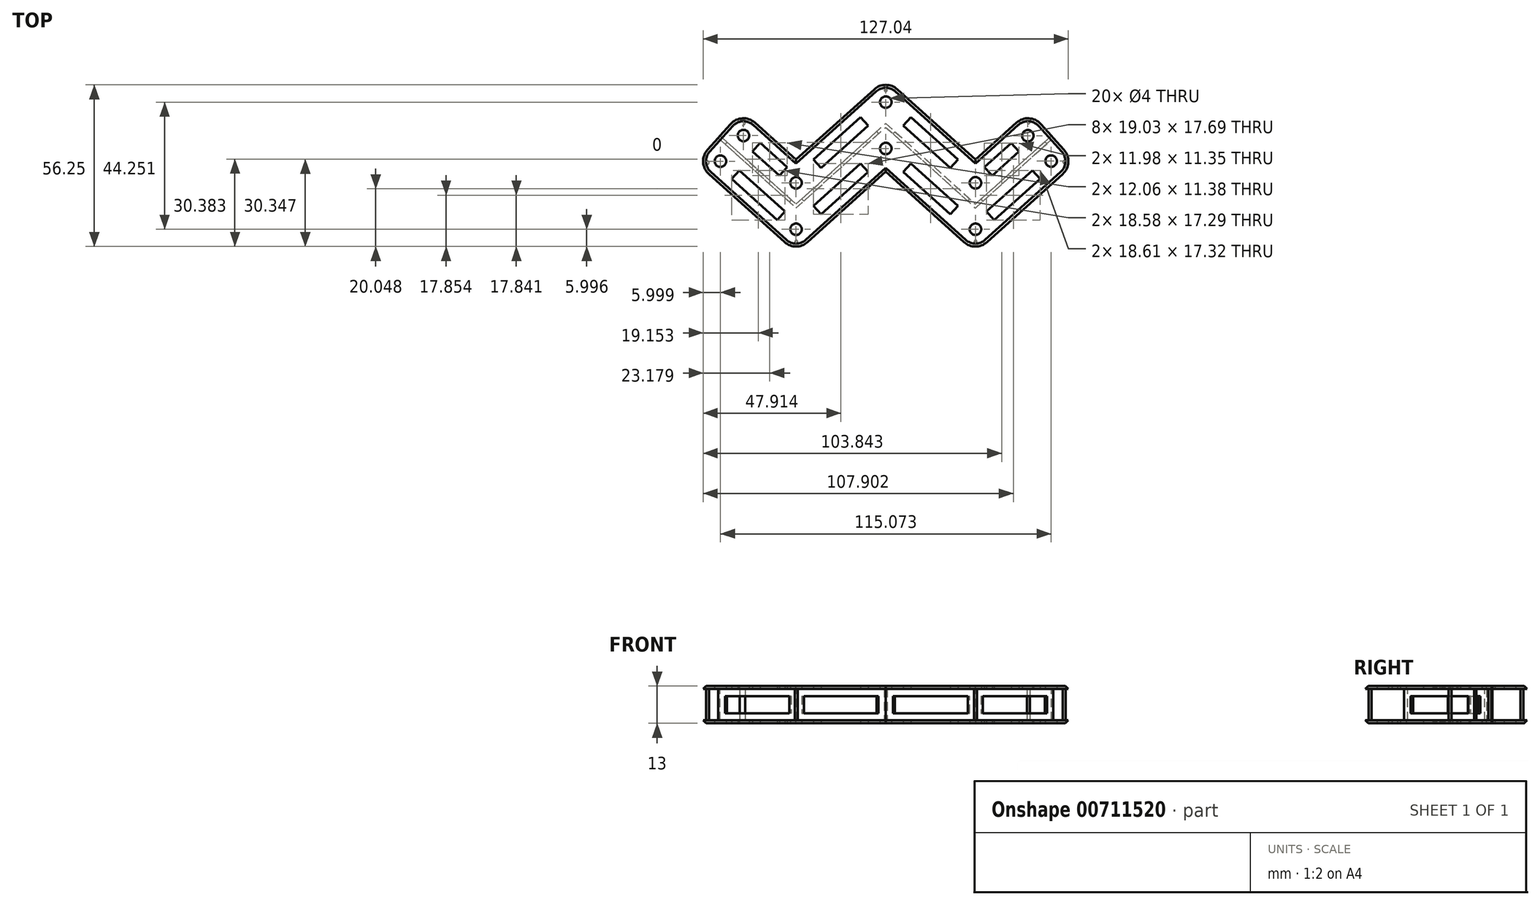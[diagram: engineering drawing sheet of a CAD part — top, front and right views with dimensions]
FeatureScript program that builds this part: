
annotation { "Feature Type Name" : "Feature", "Feature Type Description" : "" }
export const myFeature = defineFeature(function(context is Context, id is Id, definition is map)
    precondition{}
    {
        {
            var Q0;
            Q0=qCreatedBy(makeId("Top.planeOp"),FACE);
            var sketch = newSketch(context, id + "F0", { "sketchPlane" : qUnion([Q0]), "disableImprinting" : false});
            skLineSegment(sketch, "E0", {"start": v(-57.97, 24.09) * mm, "end": v(-31.21, 0) * mm});
            skLineSegment(sketch, "E1", {"start": v(-31.21, 0) * mm, "end": v(0, 28.1) * mm});
            skLineSegment(sketch, "E2", {"start": v(0, 28.1) * mm, "end": v(31.21, 0) * mm});
            skLineSegment(sketch, "E3", {"start": v(31.21, 0) * mm, "end": v(57.97, 24.09) * mm});
            skLineSegment(sketch, "E4.0", {"start": v(31.21, -0.67) * mm, "end": v(58.3, 23.72) * mm});
            skLineSegment(sketch, "E4.1", {"start": v(0, 27.43) * mm, "end": v(31.21, -0.67) * mm});
            skLineSegment(sketch, "E4.2", {"start": v(-31.21, -0.67) * mm, "end": v(0, 27.43) * mm});
            skLineSegment(sketch, "E4.3", {"start": v(-58.3, 23.72) * mm, "end": v(-31.21, -0.67) * mm});
            skLineSegment(sketch, "E5.0", {"start": v(31.21, 0.67) * mm, "end": v(57.63, 24.46) * mm});
            skLineSegment(sketch, "E5.1", {"start": v(0, 28.78) * mm, "end": v(31.21, 0.67) * mm});
            skLineSegment(sketch, "E5.2", {"start": v(-31.21, 0.67) * mm, "end": v(0, 28.78) * mm});
            skLineSegment(sketch, "E5.3", {"start": v(-57.63, 24.46) * mm, "end": v(-31.21, 0.67) * mm});
            skLineSegment(sketch, "E6", {"start": v(-58.3, 23.72) * mm, "end": v(-57.97, 24.09) * mm});
            skLineSegment(sketch, "E7", {"start": v(-57.97, 24.09) * mm, "end": v(-57.63, 24.46) * mm});
            skLineSegment(sketch, "E8", {"start": v(57.63, 24.46) * mm, "end": v(57.97, 24.09) * mm});
            skLineSegment(sketch, "E9", {"start": v(58.3, 23.72) * mm, "end": v(57.97, 24.09) * mm});
            skLineSegment(sketch, "E10.0", {"start": v(31.21, -16.15) * mm, "end": v(66, 15.17) * mm});
            skLineSegment(sketch, "E10.1", {"start": v(0, 11.96) * mm, "end": v(31.21, -16.15) * mm});
            skLineSegment(sketch, "E10.2", {"start": v(-31.21, -16.15) * mm, "end": v(0, 11.96) * mm});
            skLineSegment(sketch, "E10.3", {"start": v(-66, 15.17) * mm, "end": v(-31.21, -16.15) * mm});
            skLineSegment(sketch, "E11.0", {"start": v(31.21, 16.15) * mm, "end": v(49.94, 33) * mm});
            skLineSegment(sketch, "E11.1", {"start": v(0, 44.25) * mm, "end": v(31.21, 16.15) * mm});
            skLineSegment(sketch, "E11.2", {"start": v(-31.21, 16.15) * mm, "end": v(0, 44.25) * mm});
            skLineSegment(sketch, "E11.3", {"start": v(-49.94, 33) * mm, "end": v(-31.21, 16.15) * mm});
            skLineSegment(sketch, "E12", {"start": v(-66, 15.17) * mm, "end": v(-58.3, 23.72) * mm});
            skLineSegment(sketch, "E13", {"start": v(-49.94, 33) * mm, "end": v(-57.63, 24.46) * mm});
            skLineSegment(sketch, "E14", {"start": v(66, 15.17) * mm, "end": v(58.3, 23.72) * mm});
            skLineSegment(sketch, "E15", {"start": v(49.94, 33) * mm, "end": v(57.63, 24.46) * mm});
            skLineSegment(sketch, "E16.0", {"start": v(31.21, -8.07) * mm, "end": v(62.01, 19.66) * mm, "construction": true});
            skLineSegment(sketch, "E16.1", {"start": v(0, 20.03) * mm, "end": v(31.21, -8.07) * mm, "construction": true});
            skLineSegment(sketch, "E16.2", {"start": v(-31.21, -8.07) * mm, "end": v(0, 20.03) * mm, "construction": true});
            skLineSegment(sketch, "E16.3", {"start": v(-61.98, 19.63) * mm, "end": v(-31.21, -8.07) * mm, "construction": true});
            skLineSegment(sketch, "E17.0", {"start": v(31.21, 8.07) * mm, "end": v(53.9, 28.5) * mm, "construction": true});
            skLineSegment(sketch, "E17.1", {"start": v(0, 36.18) * mm, "end": v(31.21, 8.07) * mm, "construction": true});
            skLineSegment(sketch, "E17.2", {"start": v(-31.21, 8.07) * mm, "end": v(0, 36.18) * mm, "construction": true});
            skLineSegment(sketch, "E17.3", {"start": v(-53.95, 28.55) * mm, "end": v(-31.21, 8.07) * mm, "construction": true});
            skCircle(sketch, "E18", {"center": v(-31.21, 8.07) * mm, "radius": 2 * mm});
            skCircle(sketch, "E19", {"center": v(-31.21, -8.07) * mm, "radius": 2 * mm});
            skCircle(sketch, "E20", {"center": v(0, 20.03) * mm, "radius": 2 * mm});
            skCircle(sketch, "E21", {"center": v(0, 36.18) * mm, "radius": 2 * mm});
            skCircle(sketch, "E22", {"center": v(31.21, 8.07) * mm, "radius": 2 * mm});
            skCircle(sketch, "E23", {"center": v(31.21, -8.07) * mm, "radius": 2 * mm});
            skCircle(sketch, "E24", {"center": v(49.43, 24.48) * mm, "radius": 2 * mm});
            skCircle(sketch, "E25", {"center": v(57.55, 15.64) * mm, "radius": 2 * mm});
            skCircle(sketch, "E26", {"center": v(-57.52, 15.62) * mm, "radius": 2 * mm});
            skCircle(sketch, "E27", {"center": v(-49.5, 24.53) * mm, "radius": 2 * mm});
            skLineSegment(sketch, "E28.0", {"start": v(31.21, -10.77) * mm, "end": v(63.32, 18.14) * mm, "construction": true});
            skLineSegment(sketch, "E28.1", {"start": v(0, 17.34) * mm, "end": v(31.21, -10.77) * mm, "construction": true});
            skLineSegment(sketch, "E28.2", {"start": v(-31.21, -10.77) * mm, "end": v(0, 17.34) * mm, "construction": true});
            skLineSegment(sketch, "E28.3", {"start": v(-63.32, 18.14) * mm, "end": v(-31.21, -10.77) * mm, "construction": true});
            skLineSegment(sketch, "E29.0", {"start": v(31.21, -5.38) * mm, "end": v(60.64, 21.12) * mm, "construction": true});
            skLineSegment(sketch, "E29.1", {"start": v(0, 22.72) * mm, "end": v(31.21, -5.38) * mm, "construction": true});
            skLineSegment(sketch, "E29.2", {"start": v(-31.21, -5.38) * mm, "end": v(0, 22.72) * mm, "construction": true});
            skLineSegment(sketch, "E29.3", {"start": v(-60.64, 21.12) * mm, "end": v(-31.21, -5.38) * mm, "construction": true});
            skLineSegment(sketch, "E30.0", {"start": v(31.21, 10.77) * mm, "end": v(52.61, 30.03) * mm, "construction": true});
            skLineSegment(sketch, "E30.1", {"start": v(0, 38.87) * mm, "end": v(31.21, 10.77) * mm, "construction": true});
            skLineSegment(sketch, "E30.2", {"start": v(-31.21, 10.77) * mm, "end": v(0, 38.87) * mm, "construction": true});
            skLineSegment(sketch, "E30.3", {"start": v(-52.61, 30.03) * mm, "end": v(-31.21, 10.77) * mm, "construction": true});
            skLineSegment(sketch, "E31.0", {"start": v(31.21, 5.38) * mm, "end": v(55.29, 27.06) * mm, "construction": true});
            skLineSegment(sketch, "E31.1", {"start": v(0, 33.49) * mm, "end": v(31.21, 5.38) * mm, "construction": true});
            skLineSegment(sketch, "E31.2", {"start": v(-31.21, 5.38) * mm, "end": v(0, 33.49) * mm, "construction": true});
            skLineSegment(sketch, "E31.3", {"start": v(-55.29, 27.06) * mm, "end": v(-31.21, 5.38) * mm, "construction": true});
            skLineSegment(sketch, "E32", {"start": v(-25.12, 16.25) * mm, "end": v(-8.77, 30.97) * mm});
            skLineSegment(sketch, "E33", {"start": v(-8.77, 30.97) * mm, "end": v(-6.1, 28) * mm});
            skLineSegment(sketch, "E34", {"start": v(-25.12, 16.25) * mm, "end": v(-22.44, 13.28) * mm});
            skLineSegment(sketch, "E35", {"start": v(-22.44, 13.28) * mm, "end": v(-6.1, 28) * mm});
            skLineSegment(sketch, "E36", {"start": v(-43.7, 22) * mm, "end": v(-46.37, 19.03) * mm});
            skLineSegment(sketch, "E37", {"start": v(-46.37, 19.03) * mm, "end": v(-37.03, 10.62) * mm});
            skLineSegment(sketch, "E38", {"start": v(-37.03, 10.62) * mm, "end": v(-34.31, 13.56) * mm});
            skLineSegment(sketch, "E39", {"start": v(-34.31, 13.56) * mm, "end": v(-43.7, 22) * mm});
            skLineSegment(sketch, "E40", {"start": v(-50.98, 12.42) * mm, "end": v(-53.66, 9.44) * mm});
            skLineSegment(sketch, "E41", {"start": v(-53.66, 9.44) * mm, "end": v(-37.75, -4.88) * mm});
            skLineSegment(sketch, "E42", {"start": v(-37.75, -4.88) * mm, "end": v(-35.08, -1.9) * mm});
            skLineSegment(sketch, "E43", {"start": v(-35.08, -1.9) * mm, "end": v(-50.98, 12.42) * mm});
            skLineSegment(sketch, "E44", {"start": v(-22.44, -2.87) * mm, "end": v(-25.12, 0.1) * mm});
            skLineSegment(sketch, "E45", {"start": v(-25.12, 0.1) * mm, "end": v(-8.77, 14.82) * mm});
            skLineSegment(sketch, "E46", {"start": v(-8.77, 14.82) * mm, "end": v(-6.1, 11.85) * mm});
            skLineSegment(sketch, "E47", {"start": v(-6.1, 11.85) * mm, "end": v(-22.44, -2.87) * mm});
            skLineSegment(sketch, "E48", {"start": v(8.77, 30.97) * mm, "end": v(6.1, 28) * mm});
            skLineSegment(sketch, "E49", {"start": v(6.1, 28) * mm, "end": v(22.44, 13.28) * mm});
            skLineSegment(sketch, "E50", {"start": v(22.44, 13.28) * mm, "end": v(25.12, 16.25) * mm});
            skLineSegment(sketch, "E51", {"start": v(25.12, 16.25) * mm, "end": v(8.77, 30.97) * mm});
            skLineSegment(sketch, "E52", {"start": v(6.1, 11.85) * mm, "end": v(8.77, 14.82) * mm});
            skLineSegment(sketch, "E53", {"start": v(8.77, 14.82) * mm, "end": v(25.12, 0.1) * mm});
            skLineSegment(sketch, "E54", {"start": v(25.12, 0.1) * mm, "end": v(22.44, -2.87) * mm});
            skLineSegment(sketch, "E55", {"start": v(22.44, -2.87) * mm, "end": v(6.1, 11.85) * mm});
            skLineSegment(sketch, "E56", {"start": v(34.33, 13.57) * mm, "end": v(37, 10.6) * mm});
            skLineSegment(sketch, "E57", {"start": v(37, 10.6) * mm, "end": v(46.31, 18.98) * mm});
            skLineSegment(sketch, "E58", {"start": v(46.31, 18.98) * mm, "end": v(43.64, 21.95) * mm});
            skLineSegment(sketch, "E59", {"start": v(43.64, 21.95) * mm, "end": v(34.33, 13.57) * mm});
            skLineSegment(sketch, "E60", {"start": v(35.08, -1.9) * mm, "end": v(37.75, -4.88) * mm});
            skLineSegment(sketch, "E61", {"start": v(37.75, -4.88) * mm, "end": v(53.69, 9.47) * mm});
            skLineSegment(sketch, "E62", {"start": v(53.69, 9.47) * mm, "end": v(51.01, 12.44) * mm});
            skLineSegment(sketch, "E63", {"start": v(51.01, 12.44) * mm, "end": v(35.08, -1.9) * mm});
            skCircle(sketch, "E64", {"center": v(-61.95, 15.13) * mm, "radius": 0.5 * mm});
            skCircle(sketch, "E65", {"center": v(-49.87, 29.1) * mm, "radius": 1 * mm});
            skCircle(sketch, "E66", {"center": v(-31.12, -12.42) * mm, "radius": 0.5 * mm});
            skCircle(sketch, "E67", {"center": v(0, 40.35) * mm, "radius": 0.5 * mm});
            skCircle(sketch, "E68", {"center": v(31.26, -12.4) * mm, "radius": 0.5 * mm});
            skCircle(sketch, "E69", {"center": v(62.1, 15.36) * mm, "radius": 0.5 * mm});
            skCircle(sketch, "E70", {"center": v(49.66, 29.19) * mm, "radius": 0.5 * mm});
            skSolve(sketch);
        }
        {
            var Q0;
            Q0=makeQuery(id+"F0.imprint","IMPRINT",FACE,{"disambiguationData":[TD([[makeQuery(id+"F0.imprint","IMPRINT",EDGE,{"derivedFrom":sQuery(id+"F0.wireOp",EDGE,"E5.0")}),1.0]])]});
            var Q1;
            Q1=makeQuery(id+"F0.imprint","IMPRINT",FACE,{"disambiguationData":[TD([[makeQuery(id+"F0.imprint","IMPRINT",EDGE,{"derivedFrom":sQuery(id+"F0.wireOp",EDGE,"E4.0")}),-1.0]])]});
            var Q2;
            Q2=makeQuery(id+"F0.imprint","IMPRINT",FACE,{"disambiguationData":[TD([[makeQuery(id+"F0.imprint","IMPRINT",EDGE,{"derivedFrom":sQuery(id+"F0.wireOp",EDGE,"E0")}),1.0]])]});
            var Q3;
            Q3=makeQuery(id+"F0.imprint","IMPRINT",FACE,{"disambiguationData":[TD([[makeQuery(id+"F0.imprint","IMPRINT",EDGE,{"derivedFrom":sQuery(id+"F0.wireOp",EDGE,"E0")}),-1.0]])]});
            extrude(context, id + "F1", {"entities" : qUnion([Q0, Q1, Q2, Q3]), "depth" : 13 * mm, "offsetDistance" : 25 * mm, "symmetric" : true});
        }
        {
            var Q0;
            Q0=makeQuery(id+"F0.imprint","IMPRINT",FACE,{"disambiguationData":[TD([[makeQuery(id+"F0.imprint","IMPRINT",EDGE,{"derivedFrom":sQuery(id+"F0.wireOp",EDGE,"E5.0")}),1.0]])]});
            var Q1;
            Q1=makeQuery(id+"F0.imprint","IMPRINT",FACE,{"disambiguationData":[TD([[makeQuery(id+"F0.imprint","IMPRINT",EDGE,{"derivedFrom":sQuery(id+"F0.wireOp",EDGE,"E4.0")}),-1.0]])]});
            extrude(context, id + "F2", {"entities" : qUnion([Q0, Q1]), "operationType" : NewBodyOperationType.REMOVE, "oppositeDirection" : true, "depth" : 11 * mm, "offsetDistance" : 25 * mm, "symmetric" : true});
        }
        {
            var Q0;
            Q0=makeQuery(id+"F2.boolean.opBoolean","COPY",FACE,{"derivedFrom":makeQuery(id+"F2.opExtrude","SWEPT_FACE",FACE,{"disambiguationData":[OSD([sQuery(id+"F0.wireOp",EDGE,"E4.0")])]})});
            var sketch = newSketch(context, id + "F3", { "sketchPlane" : qUnion([Q0])});
            skLineSegment(sketch, "E71.bottom", {"start": v(26.18, 3) * mm, "end": v(56.18, 3) * mm});
            skLineSegment(sketch, "E71.top", {"start": v(26.18, -3) * mm, "end": v(56.18, -3) * mm});
            skLineSegment(sketch, "E71.left", {"start": v(26.18, 3) * mm, "end": v(26.18, -3) * mm});
            skLineSegment(sketch, "E71.right", {"start": v(56.18, 3) * mm, "end": v(56.18, -3) * mm});
            skPoint(sketch, "E71.middle", {"position": v(41.18, 0) * mm});
            skSolve(sketch);
        }
        {
            var Q0;
            Q0=makeQuery(id+"F3.imprint","IMPRINT",FACE,{"disambiguationData":[TD([[makeQuery(id+"F3.imprint","IMPRINT",EDGE,{"derivedFrom":sQuery(id+"F3.wireOp",EDGE,"E71.bottom")}),-1.0]])]});
            extrude(context, id + "F4", {"entities" : qUnion([Q0]), "operationType" : NewBodyOperationType.REMOVE, "oppositeDirection" : true, "depth" : 2 * mm, "offsetDistance" : 25 * mm, "symmetric" : true});
        }
        {
            var Q0;
            Q0=makeQuery(id+"F2.boolean.opBoolean","COPY",FACE,{"derivedFrom":makeQuery(id+"F2.opExtrude","SWEPT_FACE",FACE,{"disambiguationData":[OSD([sQuery(id+"F0.wireOp",EDGE,"E5.1")])]})});
            var sketch = newSketch(context, id + "F5", { "sketchPlane" : qUnion([Q0])});
            skLineSegment(sketch, "E72.bottom", {"start": v(-20.04, 3) * mm, "end": v(14.96, 3) * mm});
            skLineSegment(sketch, "E72.top", {"start": v(-20.04, -3) * mm, "end": v(14.96, -3) * mm});
            skLineSegment(sketch, "E72.left", {"start": v(-20.04, 3) * mm, "end": v(-20.04, -3) * mm});
            skLineSegment(sketch, "E72.right", {"start": v(14.96, 3) * mm, "end": v(14.96, -3) * mm});
            skPoint(sketch, "E72.middle", {"position": v(-2.54, 0) * mm});
            skSolve(sketch);
        }
        {
            var Q0;
            Q0=makeQuery(id+"F5.imprint","IMPRINT",FACE,{"disambiguationData":[TD([[makeQuery(id+"F5.imprint","IMPRINT",EDGE,{"derivedFrom":sQuery(id+"F5.wireOp",EDGE,"E72.bottom")}),-1.0]])]});
            extrude(context, id + "F6", {"entities" : qUnion([Q0]), "operationType" : NewBodyOperationType.REMOVE, "oppositeDirection" : true, "depth" : 3 * mm, "offsetDistance" : 25 * mm, "symmetric" : true});
        }
        {
            var Q0;
            Q0=makeQuery(id+"F2.boolean.opBoolean","COPY",FACE,{"derivedFrom":makeQuery(id+"F2.opExtrude","SWEPT_FACE",FACE,{"disambiguationData":[OSD([sQuery(id+"F0.wireOp",EDGE,"E4.2")])]})});
            var sketch = newSketch(context, id + "F7", { "sketchPlane" : qUnion([Q0])});
            skLineSegment(sketch, "E73.bottom", {"start": v(-20, 3) * mm, "end": v(15, 3) * mm});
            skLineSegment(sketch, "E73.top", {"start": v(-20, -3) * mm, "end": v(15, -3) * mm});
            skLineSegment(sketch, "E73.left", {"start": v(-20, 3) * mm, "end": v(-20, -3) * mm});
            skLineSegment(sketch, "E73.right", {"start": v(15, 3) * mm, "end": v(15, -3) * mm});
            skPoint(sketch, "E73.middle", {"position": v(-2.5, 0) * mm});
            skSolve(sketch);
        }
        {
            var Q0;
            Q0=makeQuery(id+"F7.imprint","IMPRINT",FACE,{"disambiguationData":[TD([[makeQuery(id+"F7.imprint","IMPRINT",EDGE,{"derivedFrom":sQuery(id+"F7.wireOp",EDGE,"E73.bottom")}),-1.0]])]});
            extrude(context, id + "F8", {"entities" : qUnion([Q0]), "operationType" : NewBodyOperationType.REMOVE, "oppositeDirection" : true, "depth" : 3 * mm, "offsetDistance" : 25 * mm, "symmetric" : true});
        }
        {
            var Q0;
            Q0=makeQuery(id+"F2.boolean.opBoolean","COPY",FACE,{"derivedFrom":makeQuery(id+"F2.opExtrude","SWEPT_FACE",FACE,{"disambiguationData":[OSD([sQuery(id+"F0.wireOp",EDGE,"E4.3")])]})});
            var sketch = newSketch(context, id + "F9", { "sketchPlane" : qUnion([Q0])});
            skLineSegment(sketch, "E74.bottom", {"start": v(-55.95, 3) * mm, "end": v(-25.95, 3) * mm});
            skLineSegment(sketch, "E74.top", {"start": v(-55.95, -3) * mm, "end": v(-25.95, -3) * mm});
            skLineSegment(sketch, "E74.left", {"start": v(-55.95, 3) * mm, "end": v(-55.95, -3) * mm});
            skLineSegment(sketch, "E74.right", {"start": v(-25.95, 3) * mm, "end": v(-25.95, -3) * mm});
            skPoint(sketch, "E74.middle", {"position": v(-40.95, 0) * mm});
            skSolve(sketch);
        }
        {
            var Q0;
            Q0=makeQuery(id+"F9.imprint","IMPRINT",FACE,{"disambiguationData":[TD([[makeQuery(id+"F9.imprint","IMPRINT",EDGE,{"derivedFrom":sQuery(id+"F9.wireOp",EDGE,"E74.bottom")}),-1.0]])]});
            extrude(context, id + "F10", {"entities" : qUnion([Q0]), "operationType" : NewBodyOperationType.REMOVE, "oppositeDirection" : true, "depth" : 3 * mm, "offsetDistance" : 25 * mm, "symmetric" : true});
        }
        {
            var Q0;
            {var subQ0=sQuery(id+"F0.wireOp",EDGE,"E27");var subQ1=sQuery(id+"F0.wireOp",EDGE,"E24");var subQ2=sQuery(id+"F0.wireOp",EDGE,"E22");var subQ3=sQuery(id+"F0.wireOp",EDGE,"E21");var subQ4=sQuery(id+"F0.wireOp",EDGE,"E18");var subQ5=sQuery(id+"F0.wireOp",EDGE,"E15");var subQ7=sQuery(id+"F0.wireOp",EDGE,"E13");var subQ8=sQuery(id+"F0.wireOp",EDGE,"E11.3");var subQ9=sQuery(id+"F0.wireOp",EDGE,"E11.2");var subQ10=sQuery(id+"F0.wireOp",EDGE,"E11.1");var subQ11=sQuery(id+"F0.wireOp",EDGE,"E11.0");Q0=makeQuery(id+"F2.boolean.opBoolean","SPLIT",EDGE,{"disambiguationData":[TD([makeQuery(id+"F2.opExtrude","CAP_FACE",FACE,{"disambiguationData":[OSD([sQuery(id+"F0.wireOp",EDGE,"E5.0"),sQuery(id+"F0.wireOp",EDGE,"E5.1"),sQuery(id+"F0.wireOp",EDGE,"E5.2"),sQuery(id+"F0.wireOp",EDGE,"E5.3"),subQ11,subQ10,subQ9,subQ8,subQ7,subQ5,subQ4,subQ3,subQ2,subQ1,subQ0])],"isStart":true})])],"derivedFrom":makeQuery(id+"F1.opExtrude","SWEPT_EDGE",EDGE,{"disambiguationData":[OSD([subQ11,subQ5])]})});}
            var Q1;
            {var subQ0=sQuery(id+"F0.wireOp",EDGE,"E27");var subQ1=sQuery(id+"F0.wireOp",EDGE,"E24");var subQ2=sQuery(id+"F0.wireOp",EDGE,"E22");var subQ3=sQuery(id+"F0.wireOp",EDGE,"E21");var subQ4=sQuery(id+"F0.wireOp",EDGE,"E18");var subQ5=sQuery(id+"F0.wireOp",EDGE,"E15");var subQ7=sQuery(id+"F0.wireOp",EDGE,"E13");var subQ8=sQuery(id+"F0.wireOp",EDGE,"E11.3");var subQ9=sQuery(id+"F0.wireOp",EDGE,"E11.2");var subQ10=sQuery(id+"F0.wireOp",EDGE,"E11.1");var subQ11=sQuery(id+"F0.wireOp",EDGE,"E11.0");Q1=makeQuery(id+"F2.boolean.opBoolean","SPLIT",EDGE,{"disambiguationData":[TD([makeQuery(id+"F2.opExtrude","CAP_FACE",FACE,{"disambiguationData":[OSD([sQuery(id+"F0.wireOp",EDGE,"E5.0"),sQuery(id+"F0.wireOp",EDGE,"E5.1"),sQuery(id+"F0.wireOp",EDGE,"E5.2"),sQuery(id+"F0.wireOp",EDGE,"E5.3"),subQ11,subQ10,subQ9,subQ8,subQ7,subQ5,subQ4,subQ3,subQ2,subQ1,subQ0])],"isStart":false})])],"derivedFrom":makeQuery(id+"F1.opExtrude","SWEPT_EDGE",EDGE,{"disambiguationData":[OSD([subQ11,subQ5])]})});}
            var Q2;
            {var subQ0=sQuery(id+"F0.wireOp",EDGE,"E27");var subQ1=sQuery(id+"F0.wireOp",EDGE,"E24");var subQ2=sQuery(id+"F0.wireOp",EDGE,"E22");var subQ3=sQuery(id+"F0.wireOp",EDGE,"E21");var subQ4=sQuery(id+"F0.wireOp",EDGE,"E18");var subQ5=sQuery(id+"F0.wireOp",EDGE,"E15");var subQ6=sQuery(id+"F0.wireOp",EDGE,"E13");var subQ7=sQuery(id+"F0.wireOp",EDGE,"E11.3");var subQ8=sQuery(id+"F0.wireOp",EDGE,"E11.2");var subQ9=sQuery(id+"F0.wireOp",EDGE,"E11.1");var subQ10=sQuery(id+"F0.wireOp",EDGE,"E11.0");Q2=makeQuery(id+"F2.boolean.opBoolean","SPLIT",EDGE,{"disambiguationData":[TD([makeQuery(id+"F2.opExtrude","CAP_FACE",FACE,{"disambiguationData":[OSD([sQuery(id+"F0.wireOp",EDGE,"E5.0"),sQuery(id+"F0.wireOp",EDGE,"E5.1"),sQuery(id+"F0.wireOp",EDGE,"E5.2"),sQuery(id+"F0.wireOp",EDGE,"E5.3"),subQ10,subQ9,subQ8,subQ7,subQ6,subQ5,subQ4,subQ3,subQ2,subQ1,subQ0])],"isStart":false})])],"derivedFrom":makeQuery(id+"F1.opExtrude","SWEPT_EDGE",EDGE,{"disambiguationData":[OSD([subQ9,subQ8])]})});}
            var Q3;
            {var subQ0=sQuery(id+"F0.wireOp",EDGE,"E27");var subQ1=sQuery(id+"F0.wireOp",EDGE,"E24");var subQ2=sQuery(id+"F0.wireOp",EDGE,"E22");var subQ3=sQuery(id+"F0.wireOp",EDGE,"E21");var subQ4=sQuery(id+"F0.wireOp",EDGE,"E18");var subQ5=sQuery(id+"F0.wireOp",EDGE,"E15");var subQ6=sQuery(id+"F0.wireOp",EDGE,"E13");var subQ7=sQuery(id+"F0.wireOp",EDGE,"E11.3");var subQ8=sQuery(id+"F0.wireOp",EDGE,"E11.2");var subQ9=sQuery(id+"F0.wireOp",EDGE,"E11.1");var subQ10=sQuery(id+"F0.wireOp",EDGE,"E11.0");Q3=makeQuery(id+"F2.boolean.opBoolean","SPLIT",EDGE,{"disambiguationData":[TD([makeQuery(id+"F2.opExtrude","CAP_FACE",FACE,{"disambiguationData":[OSD([sQuery(id+"F0.wireOp",EDGE,"E5.0"),sQuery(id+"F0.wireOp",EDGE,"E5.1"),sQuery(id+"F0.wireOp",EDGE,"E5.2"),sQuery(id+"F0.wireOp",EDGE,"E5.3"),subQ10,subQ9,subQ8,subQ7,subQ6,subQ5,subQ4,subQ3,subQ2,subQ1,subQ0])],"isStart":true})])],"derivedFrom":makeQuery(id+"F1.opExtrude","SWEPT_EDGE",EDGE,{"disambiguationData":[OSD([subQ9,subQ8])]})});}
            var Q4;
            {var subQ0=sQuery(id+"F0.wireOp",EDGE,"E27");var subQ1=sQuery(id+"F0.wireOp",EDGE,"E24");var subQ2=sQuery(id+"F0.wireOp",EDGE,"E22");var subQ3=sQuery(id+"F0.wireOp",EDGE,"E21");var subQ4=sQuery(id+"F0.wireOp",EDGE,"E18");var subQ5=sQuery(id+"F0.wireOp",EDGE,"E15");var subQ6=sQuery(id+"F0.wireOp",EDGE,"E13");var subQ8=sQuery(id+"F0.wireOp",EDGE,"E11.3");var subQ9=sQuery(id+"F0.wireOp",EDGE,"E11.2");var subQ10=sQuery(id+"F0.wireOp",EDGE,"E11.1");var subQ11=sQuery(id+"F0.wireOp",EDGE,"E11.0");Q4=makeQuery(id+"F2.boolean.opBoolean","SPLIT",EDGE,{"disambiguationData":[TD([makeQuery(id+"F2.opExtrude","CAP_FACE",FACE,{"disambiguationData":[OSD([sQuery(id+"F0.wireOp",EDGE,"E5.0"),sQuery(id+"F0.wireOp",EDGE,"E5.1"),sQuery(id+"F0.wireOp",EDGE,"E5.2"),sQuery(id+"F0.wireOp",EDGE,"E5.3"),subQ11,subQ10,subQ9,subQ8,subQ6,subQ5,subQ4,subQ3,subQ2,subQ1,subQ0])],"isStart":false})])],"derivedFrom":makeQuery(id+"F1.opExtrude","SWEPT_EDGE",EDGE,{"disambiguationData":[OSD([subQ8,subQ6])]})});}
            var Q5;
            {var subQ0=sQuery(id+"F0.wireOp",EDGE,"E27");var subQ1=sQuery(id+"F0.wireOp",EDGE,"E24");var subQ2=sQuery(id+"F0.wireOp",EDGE,"E22");var subQ3=sQuery(id+"F0.wireOp",EDGE,"E21");var subQ4=sQuery(id+"F0.wireOp",EDGE,"E18");var subQ5=sQuery(id+"F0.wireOp",EDGE,"E15");var subQ6=sQuery(id+"F0.wireOp",EDGE,"E13");var subQ8=sQuery(id+"F0.wireOp",EDGE,"E11.3");var subQ9=sQuery(id+"F0.wireOp",EDGE,"E11.2");var subQ10=sQuery(id+"F0.wireOp",EDGE,"E11.1");var subQ11=sQuery(id+"F0.wireOp",EDGE,"E11.0");Q5=makeQuery(id+"F2.boolean.opBoolean","SPLIT",EDGE,{"disambiguationData":[TD([makeQuery(id+"F2.opExtrude","CAP_FACE",FACE,{"disambiguationData":[OSD([sQuery(id+"F0.wireOp",EDGE,"E5.0"),sQuery(id+"F0.wireOp",EDGE,"E5.1"),sQuery(id+"F0.wireOp",EDGE,"E5.2"),sQuery(id+"F0.wireOp",EDGE,"E5.3"),subQ11,subQ10,subQ9,subQ8,subQ6,subQ5,subQ4,subQ3,subQ2,subQ1,subQ0])],"isStart":true})])],"derivedFrom":makeQuery(id+"F1.opExtrude","SWEPT_EDGE",EDGE,{"disambiguationData":[OSD([subQ8,subQ6])]})});}
            var Q6;
            {var subQ0=sQuery(id+"F0.wireOp",EDGE,"E26");var subQ1=sQuery(id+"F0.wireOp",EDGE,"E25");var subQ2=sQuery(id+"F0.wireOp",EDGE,"E23");var subQ3=sQuery(id+"F0.wireOp",EDGE,"E20");var subQ4=sQuery(id+"F0.wireOp",EDGE,"E19");var subQ5=sQuery(id+"F0.wireOp",EDGE,"E14");var subQ7=sQuery(id+"F0.wireOp",EDGE,"E12");var subQ8=sQuery(id+"F0.wireOp",EDGE,"E10.3");var subQ9=sQuery(id+"F0.wireOp",EDGE,"E10.2");var subQ10=sQuery(id+"F0.wireOp",EDGE,"E10.1");var subQ11=sQuery(id+"F0.wireOp",EDGE,"E10.0");Q6=makeQuery(id+"F2.boolean.opBoolean","SPLIT",EDGE,{"disambiguationData":[TD([makeQuery(id+"F2.opExtrude","CAP_FACE",FACE,{"disambiguationData":[OSD([sQuery(id+"F0.wireOp",EDGE,"E4.0"),sQuery(id+"F0.wireOp",EDGE,"E4.1"),sQuery(id+"F0.wireOp",EDGE,"E4.2"),sQuery(id+"F0.wireOp",EDGE,"E4.3"),subQ11,subQ10,subQ9,subQ8,subQ7,subQ5,subQ4,subQ3,subQ2,subQ1,subQ0])],"isStart":false})])],"derivedFrom":makeQuery(id+"F1.opExtrude","SWEPT_EDGE",EDGE,{"disambiguationData":[OSD([subQ8,subQ7])]})});}
            var Q7;
            {var subQ0=sQuery(id+"F0.wireOp",EDGE,"E26");var subQ1=sQuery(id+"F0.wireOp",EDGE,"E25");var subQ2=sQuery(id+"F0.wireOp",EDGE,"E23");var subQ3=sQuery(id+"F0.wireOp",EDGE,"E20");var subQ4=sQuery(id+"F0.wireOp",EDGE,"E19");var subQ5=sQuery(id+"F0.wireOp",EDGE,"E14");var subQ7=sQuery(id+"F0.wireOp",EDGE,"E12");var subQ8=sQuery(id+"F0.wireOp",EDGE,"E10.3");var subQ9=sQuery(id+"F0.wireOp",EDGE,"E10.2");var subQ10=sQuery(id+"F0.wireOp",EDGE,"E10.1");var subQ11=sQuery(id+"F0.wireOp",EDGE,"E10.0");Q7=makeQuery(id+"F2.boolean.opBoolean","SPLIT",EDGE,{"disambiguationData":[TD([makeQuery(id+"F2.opExtrude","CAP_FACE",FACE,{"disambiguationData":[OSD([sQuery(id+"F0.wireOp",EDGE,"E4.0"),sQuery(id+"F0.wireOp",EDGE,"E4.1"),sQuery(id+"F0.wireOp",EDGE,"E4.2"),sQuery(id+"F0.wireOp",EDGE,"E4.3"),subQ11,subQ10,subQ9,subQ8,subQ7,subQ5,subQ4,subQ3,subQ2,subQ1,subQ0])],"isStart":true})])],"derivedFrom":makeQuery(id+"F1.opExtrude","SWEPT_EDGE",EDGE,{"disambiguationData":[OSD([subQ8,subQ7])]})});}
            var Q8;
            {var subQ0=sQuery(id+"F0.wireOp",EDGE,"E26");var subQ1=sQuery(id+"F0.wireOp",EDGE,"E25");var subQ2=sQuery(id+"F0.wireOp",EDGE,"E23");var subQ3=sQuery(id+"F0.wireOp",EDGE,"E20");var subQ4=sQuery(id+"F0.wireOp",EDGE,"E19");var subQ5=sQuery(id+"F0.wireOp",EDGE,"E14");var subQ6=sQuery(id+"F0.wireOp",EDGE,"E12");var subQ7=sQuery(id+"F0.wireOp",EDGE,"E10.3");var subQ8=sQuery(id+"F0.wireOp",EDGE,"E10.2");var subQ9=sQuery(id+"F0.wireOp",EDGE,"E10.1");var subQ10=sQuery(id+"F0.wireOp",EDGE,"E10.0");Q8=makeQuery(id+"F2.boolean.opBoolean","SPLIT",EDGE,{"disambiguationData":[TD([makeQuery(id+"F2.opExtrude","CAP_FACE",FACE,{"disambiguationData":[OSD([sQuery(id+"F0.wireOp",EDGE,"E4.0"),sQuery(id+"F0.wireOp",EDGE,"E4.1"),sQuery(id+"F0.wireOp",EDGE,"E4.2"),sQuery(id+"F0.wireOp",EDGE,"E4.3"),subQ10,subQ9,subQ8,subQ7,subQ6,subQ5,subQ4,subQ3,subQ2,subQ1,subQ0])],"isStart":true})])],"derivedFrom":makeQuery(id+"F1.opExtrude","SWEPT_EDGE",EDGE,{"disambiguationData":[OSD([subQ8,subQ7])]})});}
            var Q9;
            {var subQ0=sQuery(id+"F0.wireOp",EDGE,"E26");var subQ1=sQuery(id+"F0.wireOp",EDGE,"E25");var subQ2=sQuery(id+"F0.wireOp",EDGE,"E23");var subQ3=sQuery(id+"F0.wireOp",EDGE,"E20");var subQ4=sQuery(id+"F0.wireOp",EDGE,"E19");var subQ5=sQuery(id+"F0.wireOp",EDGE,"E14");var subQ6=sQuery(id+"F0.wireOp",EDGE,"E12");var subQ7=sQuery(id+"F0.wireOp",EDGE,"E10.3");var subQ8=sQuery(id+"F0.wireOp",EDGE,"E10.2");var subQ9=sQuery(id+"F0.wireOp",EDGE,"E10.1");var subQ10=sQuery(id+"F0.wireOp",EDGE,"E10.0");Q9=makeQuery(id+"F2.boolean.opBoolean","SPLIT",EDGE,{"disambiguationData":[TD([makeQuery(id+"F2.opExtrude","CAP_FACE",FACE,{"disambiguationData":[OSD([sQuery(id+"F0.wireOp",EDGE,"E4.0"),sQuery(id+"F0.wireOp",EDGE,"E4.1"),sQuery(id+"F0.wireOp",EDGE,"E4.2"),sQuery(id+"F0.wireOp",EDGE,"E4.3"),subQ10,subQ9,subQ8,subQ7,subQ6,subQ5,subQ4,subQ3,subQ2,subQ1,subQ0])],"isStart":false})])],"derivedFrom":makeQuery(id+"F1.opExtrude","SWEPT_EDGE",EDGE,{"disambiguationData":[OSD([subQ8,subQ7])]})});}
            var Q10;
            {var subQ0=sQuery(id+"F0.wireOp",EDGE,"E26");var subQ1=sQuery(id+"F0.wireOp",EDGE,"E25");var subQ2=sQuery(id+"F0.wireOp",EDGE,"E23");var subQ3=sQuery(id+"F0.wireOp",EDGE,"E20");var subQ4=sQuery(id+"F0.wireOp",EDGE,"E19");var subQ5=sQuery(id+"F0.wireOp",EDGE,"E14");var subQ6=sQuery(id+"F0.wireOp",EDGE,"E12");var subQ7=sQuery(id+"F0.wireOp",EDGE,"E10.3");var subQ8=sQuery(id+"F0.wireOp",EDGE,"E10.2");var subQ9=sQuery(id+"F0.wireOp",EDGE,"E10.1");var subQ10=sQuery(id+"F0.wireOp",EDGE,"E10.0");Q10=makeQuery(id+"F2.boolean.opBoolean","SPLIT",EDGE,{"disambiguationData":[TD([makeQuery(id+"F2.opExtrude","CAP_FACE",FACE,{"disambiguationData":[OSD([sQuery(id+"F0.wireOp",EDGE,"E4.0"),sQuery(id+"F0.wireOp",EDGE,"E4.1"),sQuery(id+"F0.wireOp",EDGE,"E4.2"),sQuery(id+"F0.wireOp",EDGE,"E4.3"),subQ10,subQ9,subQ8,subQ7,subQ6,subQ5,subQ4,subQ3,subQ2,subQ1,subQ0])],"isStart":true})])],"derivedFrom":makeQuery(id+"F1.opExtrude","SWEPT_EDGE",EDGE,{"disambiguationData":[OSD([subQ10,subQ9])]})});}
            var Q11;
            {var subQ0=sQuery(id+"F0.wireOp",EDGE,"E26");var subQ1=sQuery(id+"F0.wireOp",EDGE,"E25");var subQ2=sQuery(id+"F0.wireOp",EDGE,"E23");var subQ3=sQuery(id+"F0.wireOp",EDGE,"E20");var subQ4=sQuery(id+"F0.wireOp",EDGE,"E19");var subQ5=sQuery(id+"F0.wireOp",EDGE,"E14");var subQ6=sQuery(id+"F0.wireOp",EDGE,"E12");var subQ7=sQuery(id+"F0.wireOp",EDGE,"E10.3");var subQ8=sQuery(id+"F0.wireOp",EDGE,"E10.2");var subQ9=sQuery(id+"F0.wireOp",EDGE,"E10.1");var subQ10=sQuery(id+"F0.wireOp",EDGE,"E10.0");Q11=makeQuery(id+"F2.boolean.opBoolean","SPLIT",EDGE,{"disambiguationData":[TD([makeQuery(id+"F2.opExtrude","CAP_FACE",FACE,{"disambiguationData":[OSD([sQuery(id+"F0.wireOp",EDGE,"E4.0"),sQuery(id+"F0.wireOp",EDGE,"E4.1"),sQuery(id+"F0.wireOp",EDGE,"E4.2"),sQuery(id+"F0.wireOp",EDGE,"E4.3"),subQ10,subQ9,subQ8,subQ7,subQ6,subQ5,subQ4,subQ3,subQ2,subQ1,subQ0])],"isStart":false})])],"derivedFrom":makeQuery(id+"F1.opExtrude","SWEPT_EDGE",EDGE,{"disambiguationData":[OSD([subQ10,subQ9])]})});}
            var Q12;
            {var subQ0=sQuery(id+"F0.wireOp",EDGE,"E26");var subQ1=sQuery(id+"F0.wireOp",EDGE,"E25");var subQ2=sQuery(id+"F0.wireOp",EDGE,"E23");var subQ3=sQuery(id+"F0.wireOp",EDGE,"E20");var subQ4=sQuery(id+"F0.wireOp",EDGE,"E19");var subQ6=sQuery(id+"F0.wireOp",EDGE,"E14");var subQ7=sQuery(id+"F0.wireOp",EDGE,"E12");var subQ8=sQuery(id+"F0.wireOp",EDGE,"E10.3");var subQ9=sQuery(id+"F0.wireOp",EDGE,"E10.2");var subQ10=sQuery(id+"F0.wireOp",EDGE,"E10.1");var subQ11=sQuery(id+"F0.wireOp",EDGE,"E10.0");Q12=makeQuery(id+"F2.boolean.opBoolean","SPLIT",EDGE,{"disambiguationData":[TD([makeQuery(id+"F2.opExtrude","CAP_FACE",FACE,{"disambiguationData":[OSD([sQuery(id+"F0.wireOp",EDGE,"E4.0"),sQuery(id+"F0.wireOp",EDGE,"E4.1"),sQuery(id+"F0.wireOp",EDGE,"E4.2"),sQuery(id+"F0.wireOp",EDGE,"E4.3"),subQ11,subQ10,subQ9,subQ8,subQ7,subQ6,subQ4,subQ3,subQ2,subQ1,subQ0])],"isStart":false})])],"derivedFrom":makeQuery(id+"F1.opExtrude","SWEPT_EDGE",EDGE,{"disambiguationData":[OSD([subQ11,subQ6])]})});}
            var Q13;
            {var subQ0=sQuery(id+"F0.wireOp",EDGE,"E26");var subQ1=sQuery(id+"F0.wireOp",EDGE,"E25");var subQ2=sQuery(id+"F0.wireOp",EDGE,"E23");var subQ3=sQuery(id+"F0.wireOp",EDGE,"E20");var subQ4=sQuery(id+"F0.wireOp",EDGE,"E19");var subQ6=sQuery(id+"F0.wireOp",EDGE,"E14");var subQ7=sQuery(id+"F0.wireOp",EDGE,"E12");var subQ8=sQuery(id+"F0.wireOp",EDGE,"E10.3");var subQ9=sQuery(id+"F0.wireOp",EDGE,"E10.2");var subQ10=sQuery(id+"F0.wireOp",EDGE,"E10.1");var subQ11=sQuery(id+"F0.wireOp",EDGE,"E10.0");Q13=makeQuery(id+"F2.boolean.opBoolean","SPLIT",EDGE,{"disambiguationData":[TD([makeQuery(id+"F2.opExtrude","CAP_FACE",FACE,{"disambiguationData":[OSD([sQuery(id+"F0.wireOp",EDGE,"E4.0"),sQuery(id+"F0.wireOp",EDGE,"E4.1"),sQuery(id+"F0.wireOp",EDGE,"E4.2"),sQuery(id+"F0.wireOp",EDGE,"E4.3"),subQ11,subQ10,subQ9,subQ8,subQ7,subQ6,subQ4,subQ3,subQ2,subQ1,subQ0])],"isStart":true})])],"derivedFrom":makeQuery(id+"F1.opExtrude","SWEPT_EDGE",EDGE,{"disambiguationData":[OSD([subQ11,subQ6])]})});}
            fillet(context, id + "F11", {"entities" : qUnion([Q0, Q1, Q2, Q3, Q4, Q5, Q6, Q7, Q8, Q9, Q10, Q11, Q12, Q13]), "radius" : 6 * mm, "tangentPropagation" : true, "allowEdgeOverflow" : false});
        }
        {
            var Q0;
            Q0=makeQuery(id+"F0.imprint","IMPRINT",FACE,{"disambiguationData":[TD([[makeQuery(id+"F0.imprint","IMPRINT",EDGE,{"derivedFrom":sQuery(id+"F0.wireOp",EDGE,"E69")}),1.0]])]});
            var Q1;
            Q1=makeQuery(id+"F0.imprint","IMPRINT",FACE,{"disambiguationData":[TD([[makeQuery(id+"F0.imprint","IMPRINT",EDGE,{"derivedFrom":sQuery(id+"F0.wireOp",EDGE,"E70")}),1.0]])]});
            var Q2;
            Q2=makeQuery(id+"F0.imprint","IMPRINT",FACE,{"disambiguationData":[TD([[makeQuery(id+"F0.imprint","IMPRINT",EDGE,{"derivedFrom":sQuery(id+"F0.wireOp",EDGE,"E67")}),1.0]])]});
            var Q3;
            Q3=makeQuery(id+"F0.imprint","IMPRINT",FACE,{"disambiguationData":[TD([[makeQuery(id+"F0.imprint","IMPRINT",EDGE,{"derivedFrom":sQuery(id+"F0.wireOp",EDGE,"E68")}),1.0]])]});
            var Q4;
            Q4=makeQuery(id+"F0.imprint","IMPRINT",FACE,{"disambiguationData":[TD([[makeQuery(id+"F0.imprint","IMPRINT",EDGE,{"derivedFrom":sQuery(id+"F0.wireOp",EDGE,"E66")}),1.0]])]});
            var Q5;
            Q5=makeQuery(id+"F0.imprint","IMPRINT",FACE,{"disambiguationData":[TD([[makeQuery(id+"F0.imprint","IMPRINT",EDGE,{"derivedFrom":sQuery(id+"F0.wireOp",EDGE,"E65")}),1.0]])]});
            var Q6;
            Q6=makeQuery(id+"F0.imprint","IMPRINT",FACE,{"disambiguationData":[TD([[makeQuery(id+"F0.imprint","IMPRINT",EDGE,{"derivedFrom":sQuery(id+"F0.wireOp",EDGE,"E64")}),1.0]])]});
            extrude(context, id + "F12", {"entities" : qUnion([Q0, Q1, Q2, Q3, Q4, Q5, Q6]), "operationType" : NewBodyOperationType.ADD, "depth" : 13 * mm, "offsetDistance" : 25 * mm, "symmetric" : true});
        }
        {
            var Q0;
            Q0=makeQuery(id+"F1.opExtrude","CAP_EDGE",EDGE,{"disambiguationData":[OSD([sQuery(id+"F0.wireOp",EDGE,"E10.3")])],"isStart":false});
            var Q1;
            {var subQ0=sQuery(id+"F0.wireOp",EDGE,"E69");var subQ1=sQuery(id+"F0.wireOp",EDGE,"E68");var subQ2=sQuery(id+"F0.wireOp",EDGE,"E66");var subQ3=sQuery(id+"F0.wireOp",EDGE,"E64");var subQ4=sQuery(id+"F0.wireOp",EDGE,"E63");var subQ5=sQuery(id+"F0.wireOp",EDGE,"E62");var subQ6=sQuery(id+"F0.wireOp",EDGE,"E61");var subQ7=sQuery(id+"F0.wireOp",EDGE,"E60");var subQ8=sQuery(id+"F0.wireOp",EDGE,"E55");var subQ9=sQuery(id+"F0.wireOp",EDGE,"E54");var subQ10=sQuery(id+"F0.wireOp",EDGE,"E53");var subQ11=sQuery(id+"F0.wireOp",EDGE,"E52");var subQ12=sQuery(id+"F0.wireOp",EDGE,"E47");var subQ13=sQuery(id+"F0.wireOp",EDGE,"E46");var subQ14=sQuery(id+"F0.wireOp",EDGE,"E45");var subQ15=sQuery(id+"F0.wireOp",EDGE,"E44");var subQ16=sQuery(id+"F0.wireOp",EDGE,"E43");var subQ17=sQuery(id+"F0.wireOp",EDGE,"E42");var subQ18=sQuery(id+"F0.wireOp",EDGE,"E41");var subQ19=sQuery(id+"F0.wireOp",EDGE,"E40");var subQ20=sQuery(id+"F0.wireOp",EDGE,"E26");var subQ21=sQuery(id+"F0.wireOp",EDGE,"E25");var subQ22=sQuery(id+"F0.wireOp",EDGE,"E23");var subQ23=sQuery(id+"F0.wireOp",EDGE,"E20");var subQ24=sQuery(id+"F0.wireOp",EDGE,"E19");var subQ25=sQuery(id+"F0.wireOp",EDGE,"E14");var subQ26=sQuery(id+"F0.wireOp",EDGE,"E12");var subQ27=sQuery(id+"F0.wireOp",EDGE,"E10.3");var subQ28=sQuery(id+"F0.wireOp",EDGE,"E10.2");var subQ29=sQuery(id+"F0.wireOp",EDGE,"E10.1");var subQ30=sQuery(id+"F0.wireOp",EDGE,"E10.0");var subQ31=makeQuery(id+"F1.opExtrude","CAP_FACE",FACE,{"disambiguationData":[OSD([sQuery(id+"F0.wireOp",EDGE,"E6"),sQuery(id+"F0.wireOp",EDGE,"E7"),sQuery(id+"F0.wireOp",EDGE,"E8"),sQuery(id+"F0.wireOp",EDGE,"E9"),subQ30,subQ29,subQ28,subQ27,sQuery(id+"F0.wireOp",EDGE,"E11.0"),sQuery(id+"F0.wireOp",EDGE,"E11.1"),sQuery(id+"F0.wireOp",EDGE,"E11.2"),sQuery(id+"F0.wireOp",EDGE,"E11.3"),subQ26,sQuery(id+"F0.wireOp",EDGE,"E13"),subQ25,sQuery(id+"F0.wireOp",EDGE,"E15"),sQuery(id+"F0.wireOp",EDGE,"E18"),subQ24,subQ23,sQuery(id+"F0.wireOp",EDGE,"E21"),sQuery(id+"F0.wireOp",EDGE,"E22"),subQ22,sQuery(id+"F0.wireOp",EDGE,"E24"),subQ21,subQ20,sQuery(id+"F0.wireOp",EDGE,"E27"),sQuery(id+"F0.wireOp",EDGE,"E32"),sQuery(id+"F0.wireOp",EDGE,"E33"),sQuery(id+"F0.wireOp",EDGE,"E34"),sQuery(id+"F0.wireOp",EDGE,"E35"),sQuery(id+"F0.wireOp",EDGE,"E36"),sQuery(id+"F0.wireOp",EDGE,"E37"),sQuery(id+"F0.wireOp",EDGE,"E38"),sQuery(id+"F0.wireOp",EDGE,"E39"),subQ19,subQ18,subQ17,subQ16,subQ15,subQ14,subQ13,subQ12,sQuery(id+"F0.wireOp",EDGE,"E48"),sQuery(id+"F0.wireOp",EDGE,"E49"),sQuery(id+"F0.wireOp",EDGE,"E50"),sQuery(id+"F0.wireOp",EDGE,"E51"),subQ11,subQ10,subQ9,subQ8,sQuery(id+"F0.wireOp",EDGE,"E56"),sQuery(id+"F0.wireOp",EDGE,"E57"),sQuery(id+"F0.wireOp",EDGE,"E58"),sQuery(id+"F0.wireOp",EDGE,"E59"),subQ7,subQ6,subQ5,subQ4,subQ3,sQuery(id+"F0.wireOp",EDGE,"E65"),subQ2,sQuery(id+"F0.wireOp",EDGE,"E67"),subQ1,subQ0,sQuery(id+"F0.wireOp",EDGE,"E70")])],"isStart":false});Q1=makeQuery(id+"F11.opFillet","BLEND_EDGE",EDGE,{"blendedFrom":[makeQuery(id+"F2.boolean.opBoolean","SPLIT",EDGE,{"disambiguationData":[TD([makeQuery(id+"F2.opExtrude","CAP_FACE",FACE,{"disambiguationData":[OSD([sQuery(id+"F0.wireOp",EDGE,"E4.0"),sQuery(id+"F0.wireOp",EDGE,"E4.1"),sQuery(id+"F0.wireOp",EDGE,"E4.2"),sQuery(id+"F0.wireOp",EDGE,"E4.3"),subQ30,subQ29,subQ28,subQ27,subQ26,subQ25,subQ24,subQ23,subQ22,subQ21,subQ20,subQ19,subQ18,subQ17,subQ16,subQ15,subQ14,subQ13,subQ12,subQ11,subQ10,subQ9,subQ8,subQ7,subQ6,subQ5,subQ4,subQ3,subQ2,subQ1,subQ0])],"isStart":true})])],"derivedFrom":makeQuery(id+"F1.opExtrude","SWEPT_EDGE",EDGE,{"disambiguationData":[OSD([subQ28,subQ27])]})}),subQ31],"blendedInto":[subQ31]});}
            var Q2;
            Q2=makeQuery(id+"F1.opExtrude","CAP_EDGE",EDGE,{"disambiguationData":[OSD([sQuery(id+"F0.wireOp",EDGE,"E10.2")])],"isStart":false});
            var Q3;
            Q3=makeQuery(id+"F1.opExtrude","CAP_EDGE",EDGE,{"disambiguationData":[OSD([sQuery(id+"F0.wireOp",EDGE,"E10.1")])],"isStart":false});
            var Q4;
            {var subQ0=sQuery(id+"F0.wireOp",EDGE,"E69");var subQ1=sQuery(id+"F0.wireOp",EDGE,"E68");var subQ2=sQuery(id+"F0.wireOp",EDGE,"E66");var subQ3=sQuery(id+"F0.wireOp",EDGE,"E64");var subQ4=sQuery(id+"F0.wireOp",EDGE,"E63");var subQ5=sQuery(id+"F0.wireOp",EDGE,"E62");var subQ6=sQuery(id+"F0.wireOp",EDGE,"E61");var subQ7=sQuery(id+"F0.wireOp",EDGE,"E60");var subQ8=sQuery(id+"F0.wireOp",EDGE,"E55");var subQ9=sQuery(id+"F0.wireOp",EDGE,"E54");var subQ10=sQuery(id+"F0.wireOp",EDGE,"E53");var subQ11=sQuery(id+"F0.wireOp",EDGE,"E52");var subQ12=sQuery(id+"F0.wireOp",EDGE,"E47");var subQ13=sQuery(id+"F0.wireOp",EDGE,"E46");var subQ14=sQuery(id+"F0.wireOp",EDGE,"E45");var subQ15=sQuery(id+"F0.wireOp",EDGE,"E44");var subQ16=sQuery(id+"F0.wireOp",EDGE,"E43");var subQ17=sQuery(id+"F0.wireOp",EDGE,"E42");var subQ18=sQuery(id+"F0.wireOp",EDGE,"E41");var subQ19=sQuery(id+"F0.wireOp",EDGE,"E40");var subQ20=sQuery(id+"F0.wireOp",EDGE,"E26");var subQ21=sQuery(id+"F0.wireOp",EDGE,"E25");var subQ22=sQuery(id+"F0.wireOp",EDGE,"E23");var subQ23=sQuery(id+"F0.wireOp",EDGE,"E20");var subQ24=sQuery(id+"F0.wireOp",EDGE,"E19");var subQ25=sQuery(id+"F0.wireOp",EDGE,"E14");var subQ26=sQuery(id+"F0.wireOp",EDGE,"E12");var subQ27=sQuery(id+"F0.wireOp",EDGE,"E10.3");var subQ28=sQuery(id+"F0.wireOp",EDGE,"E10.2");var subQ29=sQuery(id+"F0.wireOp",EDGE,"E10.1");var subQ30=sQuery(id+"F0.wireOp",EDGE,"E10.0");var subQ31=makeQuery(id+"F1.opExtrude","CAP_FACE",FACE,{"disambiguationData":[OSD([sQuery(id+"F0.wireOp",EDGE,"E6"),sQuery(id+"F0.wireOp",EDGE,"E7"),sQuery(id+"F0.wireOp",EDGE,"E8"),sQuery(id+"F0.wireOp",EDGE,"E9"),subQ30,subQ29,subQ28,subQ27,sQuery(id+"F0.wireOp",EDGE,"E11.0"),sQuery(id+"F0.wireOp",EDGE,"E11.1"),sQuery(id+"F0.wireOp",EDGE,"E11.2"),sQuery(id+"F0.wireOp",EDGE,"E11.3"),subQ26,sQuery(id+"F0.wireOp",EDGE,"E13"),subQ25,sQuery(id+"F0.wireOp",EDGE,"E15"),sQuery(id+"F0.wireOp",EDGE,"E18"),subQ24,subQ23,sQuery(id+"F0.wireOp",EDGE,"E21"),sQuery(id+"F0.wireOp",EDGE,"E22"),subQ22,sQuery(id+"F0.wireOp",EDGE,"E24"),subQ21,subQ20,sQuery(id+"F0.wireOp",EDGE,"E27"),sQuery(id+"F0.wireOp",EDGE,"E32"),sQuery(id+"F0.wireOp",EDGE,"E33"),sQuery(id+"F0.wireOp",EDGE,"E34"),sQuery(id+"F0.wireOp",EDGE,"E35"),sQuery(id+"F0.wireOp",EDGE,"E36"),sQuery(id+"F0.wireOp",EDGE,"E37"),sQuery(id+"F0.wireOp",EDGE,"E38"),sQuery(id+"F0.wireOp",EDGE,"E39"),subQ19,subQ18,subQ17,subQ16,subQ15,subQ14,subQ13,subQ12,sQuery(id+"F0.wireOp",EDGE,"E48"),sQuery(id+"F0.wireOp",EDGE,"E49"),sQuery(id+"F0.wireOp",EDGE,"E50"),sQuery(id+"F0.wireOp",EDGE,"E51"),subQ11,subQ10,subQ9,subQ8,sQuery(id+"F0.wireOp",EDGE,"E56"),sQuery(id+"F0.wireOp",EDGE,"E57"),sQuery(id+"F0.wireOp",EDGE,"E58"),sQuery(id+"F0.wireOp",EDGE,"E59"),subQ7,subQ6,subQ5,subQ4,subQ3,sQuery(id+"F0.wireOp",EDGE,"E65"),subQ2,sQuery(id+"F0.wireOp",EDGE,"E67"),subQ1,subQ0,sQuery(id+"F0.wireOp",EDGE,"E70")])],"isStart":false});Q4=makeQuery(id+"F11.opFillet","BLEND_EDGE",EDGE,{"blendedFrom":[makeQuery(id+"F2.boolean.opBoolean","SPLIT",EDGE,{"disambiguationData":[TD([makeQuery(id+"F2.opExtrude","CAP_FACE",FACE,{"disambiguationData":[OSD([sQuery(id+"F0.wireOp",EDGE,"E4.0"),sQuery(id+"F0.wireOp",EDGE,"E4.1"),sQuery(id+"F0.wireOp",EDGE,"E4.2"),sQuery(id+"F0.wireOp",EDGE,"E4.3"),subQ30,subQ29,subQ28,subQ27,subQ26,subQ25,subQ24,subQ23,subQ22,subQ21,subQ20,subQ19,subQ18,subQ17,subQ16,subQ15,subQ14,subQ13,subQ12,subQ11,subQ10,subQ9,subQ8,subQ7,subQ6,subQ5,subQ4,subQ3,subQ2,subQ1,subQ0])],"isStart":true})])],"derivedFrom":makeQuery(id+"F1.opExtrude","SWEPT_EDGE",EDGE,{"disambiguationData":[OSD([subQ30,subQ29])]})}),subQ31],"blendedInto":[subQ31]});}
            var Q5;
            Q5=makeQuery(id+"F1.opExtrude","CAP_EDGE",EDGE,{"disambiguationData":[OSD([sQuery(id+"F0.wireOp",EDGE,"E10.0")])],"isStart":false});
            var Q6;
            {var subQ0=sQuery(id+"F0.wireOp",EDGE,"E69");var subQ1=sQuery(id+"F0.wireOp",EDGE,"E68");var subQ2=sQuery(id+"F0.wireOp",EDGE,"E66");var subQ3=sQuery(id+"F0.wireOp",EDGE,"E64");var subQ4=sQuery(id+"F0.wireOp",EDGE,"E63");var subQ5=sQuery(id+"F0.wireOp",EDGE,"E62");var subQ6=sQuery(id+"F0.wireOp",EDGE,"E61");var subQ7=sQuery(id+"F0.wireOp",EDGE,"E60");var subQ8=sQuery(id+"F0.wireOp",EDGE,"E55");var subQ9=sQuery(id+"F0.wireOp",EDGE,"E54");var subQ10=sQuery(id+"F0.wireOp",EDGE,"E53");var subQ11=sQuery(id+"F0.wireOp",EDGE,"E52");var subQ12=sQuery(id+"F0.wireOp",EDGE,"E47");var subQ13=sQuery(id+"F0.wireOp",EDGE,"E46");var subQ14=sQuery(id+"F0.wireOp",EDGE,"E45");var subQ15=sQuery(id+"F0.wireOp",EDGE,"E44");var subQ16=sQuery(id+"F0.wireOp",EDGE,"E43");var subQ17=sQuery(id+"F0.wireOp",EDGE,"E42");var subQ18=sQuery(id+"F0.wireOp",EDGE,"E41");var subQ19=sQuery(id+"F0.wireOp",EDGE,"E40");var subQ20=sQuery(id+"F0.wireOp",EDGE,"E26");var subQ21=sQuery(id+"F0.wireOp",EDGE,"E25");var subQ22=sQuery(id+"F0.wireOp",EDGE,"E23");var subQ23=sQuery(id+"F0.wireOp",EDGE,"E20");var subQ24=sQuery(id+"F0.wireOp",EDGE,"E19");var subQ25=sQuery(id+"F0.wireOp",EDGE,"E15");var subQ26=sQuery(id+"F0.wireOp",EDGE,"E14");var subQ27=sQuery(id+"F0.wireOp",EDGE,"E12");var subQ28=sQuery(id+"F0.wireOp",EDGE,"E10.3");var subQ29=sQuery(id+"F0.wireOp",EDGE,"E10.2");var subQ30=sQuery(id+"F0.wireOp",EDGE,"E10.1");var subQ31=sQuery(id+"F0.wireOp",EDGE,"E10.0");var subQ32=sQuery(id+"F0.wireOp",EDGE,"E9");var subQ33=sQuery(id+"F0.wireOp",EDGE,"E8");var subQ34=makeQuery(id+"F1.opExtrude","CAP_FACE",FACE,{"disambiguationData":[OSD([sQuery(id+"F0.wireOp",EDGE,"E6"),sQuery(id+"F0.wireOp",EDGE,"E7"),subQ33,subQ32,subQ31,subQ30,subQ29,subQ28,sQuery(id+"F0.wireOp",EDGE,"E11.0"),sQuery(id+"F0.wireOp",EDGE,"E11.1"),sQuery(id+"F0.wireOp",EDGE,"E11.2"),sQuery(id+"F0.wireOp",EDGE,"E11.3"),subQ27,sQuery(id+"F0.wireOp",EDGE,"E13"),subQ26,subQ25,sQuery(id+"F0.wireOp",EDGE,"E18"),subQ24,subQ23,sQuery(id+"F0.wireOp",EDGE,"E21"),sQuery(id+"F0.wireOp",EDGE,"E22"),subQ22,sQuery(id+"F0.wireOp",EDGE,"E24"),subQ21,subQ20,sQuery(id+"F0.wireOp",EDGE,"E27"),sQuery(id+"F0.wireOp",EDGE,"E32"),sQuery(id+"F0.wireOp",EDGE,"E33"),sQuery(id+"F0.wireOp",EDGE,"E34"),sQuery(id+"F0.wireOp",EDGE,"E35"),sQuery(id+"F0.wireOp",EDGE,"E36"),sQuery(id+"F0.wireOp",EDGE,"E37"),sQuery(id+"F0.wireOp",EDGE,"E38"),sQuery(id+"F0.wireOp",EDGE,"E39"),subQ19,subQ18,subQ17,subQ16,subQ15,subQ14,subQ13,subQ12,sQuery(id+"F0.wireOp",EDGE,"E48"),sQuery(id+"F0.wireOp",EDGE,"E49"),sQuery(id+"F0.wireOp",EDGE,"E50"),sQuery(id+"F0.wireOp",EDGE,"E51"),subQ11,subQ10,subQ9,subQ8,sQuery(id+"F0.wireOp",EDGE,"E56"),sQuery(id+"F0.wireOp",EDGE,"E57"),sQuery(id+"F0.wireOp",EDGE,"E58"),sQuery(id+"F0.wireOp",EDGE,"E59"),subQ7,subQ6,subQ5,subQ4,subQ3,sQuery(id+"F0.wireOp",EDGE,"E65"),subQ2,sQuery(id+"F0.wireOp",EDGE,"E67"),subQ1,subQ0,sQuery(id+"F0.wireOp",EDGE,"E70")])],"isStart":false});Q6=makeQuery(id+"F11.opFillet","BLEND_EDGE",EDGE,{"blendedFrom":[makeQuery(id+"F2.boolean.opBoolean","SPLIT",EDGE,{"disambiguationData":[TD([makeQuery(id+"F2.opExtrude","CAP_FACE",FACE,{"disambiguationData":[OSD([sQuery(id+"F0.wireOp",EDGE,"E4.0"),sQuery(id+"F0.wireOp",EDGE,"E4.1"),sQuery(id+"F0.wireOp",EDGE,"E4.2"),sQuery(id+"F0.wireOp",EDGE,"E4.3"),subQ31,subQ30,subQ29,subQ28,subQ27,subQ26,subQ24,subQ23,subQ22,subQ21,subQ20,subQ19,subQ18,subQ17,subQ16,subQ15,subQ14,subQ13,subQ12,subQ11,subQ10,subQ9,subQ8,subQ7,subQ6,subQ5,subQ4,subQ3,subQ2,subQ1,subQ0])],"isStart":true})])],"derivedFrom":makeQuery(id+"F1.opExtrude","SWEPT_EDGE",EDGE,{"disambiguationData":[OSD([subQ31,subQ26])]})}),subQ34],"blendedInto":[subQ34]});}
            var Q7;
            Q7=makeQuery(id+"F1.opExtrude","CAP_EDGE",EDGE,{"disambiguationData":[OSD([sQuery(id+"F0.wireOp",EDGE,"E8"),sQuery(id+"F0.wireOp",EDGE,"E9"),sQuery(id+"F0.wireOp",EDGE,"E14"),sQuery(id+"F0.wireOp",EDGE,"E15")])],"isStart":false});
            var Q8;
            {var subQ0=sQuery(id+"F0.wireOp",EDGE,"E70");var subQ1=sQuery(id+"F0.wireOp",EDGE,"E67");var subQ2=sQuery(id+"F0.wireOp",EDGE,"E65");var subQ3=sQuery(id+"F0.wireOp",EDGE,"E59");var subQ4=sQuery(id+"F0.wireOp",EDGE,"E58");var subQ5=sQuery(id+"F0.wireOp",EDGE,"E57");var subQ6=sQuery(id+"F0.wireOp",EDGE,"E56");var subQ7=sQuery(id+"F0.wireOp",EDGE,"E51");var subQ8=sQuery(id+"F0.wireOp",EDGE,"E50");var subQ9=sQuery(id+"F0.wireOp",EDGE,"E49");var subQ10=sQuery(id+"F0.wireOp",EDGE,"E48");var subQ11=sQuery(id+"F0.wireOp",EDGE,"E39");var subQ12=sQuery(id+"F0.wireOp",EDGE,"E38");var subQ13=sQuery(id+"F0.wireOp",EDGE,"E37");var subQ14=sQuery(id+"F0.wireOp",EDGE,"E36");var subQ15=sQuery(id+"F0.wireOp",EDGE,"E35");var subQ16=sQuery(id+"F0.wireOp",EDGE,"E34");var subQ17=sQuery(id+"F0.wireOp",EDGE,"E33");var subQ18=sQuery(id+"F0.wireOp",EDGE,"E32");var subQ19=sQuery(id+"F0.wireOp",EDGE,"E27");var subQ20=sQuery(id+"F0.wireOp",EDGE,"E24");var subQ21=sQuery(id+"F0.wireOp",EDGE,"E22");var subQ22=sQuery(id+"F0.wireOp",EDGE,"E21");var subQ23=sQuery(id+"F0.wireOp",EDGE,"E18");var subQ24=sQuery(id+"F0.wireOp",EDGE,"E15");var subQ25=sQuery(id+"F0.wireOp",EDGE,"E14");var subQ26=sQuery(id+"F0.wireOp",EDGE,"E13");var subQ27=sQuery(id+"F0.wireOp",EDGE,"E11.3");var subQ28=sQuery(id+"F0.wireOp",EDGE,"E11.2");var subQ29=sQuery(id+"F0.wireOp",EDGE,"E11.1");var subQ30=sQuery(id+"F0.wireOp",EDGE,"E11.0");var subQ31=sQuery(id+"F0.wireOp",EDGE,"E9");var subQ32=sQuery(id+"F0.wireOp",EDGE,"E8");var subQ33=makeQuery(id+"F1.opExtrude","CAP_FACE",FACE,{"disambiguationData":[OSD([sQuery(id+"F0.wireOp",EDGE,"E6"),sQuery(id+"F0.wireOp",EDGE,"E7"),subQ32,subQ31,sQuery(id+"F0.wireOp",EDGE,"E10.0"),sQuery(id+"F0.wireOp",EDGE,"E10.1"),sQuery(id+"F0.wireOp",EDGE,"E10.2"),sQuery(id+"F0.wireOp",EDGE,"E10.3"),subQ30,subQ29,subQ28,subQ27,sQuery(id+"F0.wireOp",EDGE,"E12"),subQ26,subQ25,subQ24,subQ23,sQuery(id+"F0.wireOp",EDGE,"E19"),sQuery(id+"F0.wireOp",EDGE,"E20"),subQ22,subQ21,sQuery(id+"F0.wireOp",EDGE,"E23"),subQ20,sQuery(id+"F0.wireOp",EDGE,"E25"),sQuery(id+"F0.wireOp",EDGE,"E26"),subQ19,subQ18,subQ17,subQ16,subQ15,subQ14,subQ13,subQ12,subQ11,sQuery(id+"F0.wireOp",EDGE,"E40"),sQuery(id+"F0.wireOp",EDGE,"E41"),sQuery(id+"F0.wireOp",EDGE,"E42"),sQuery(id+"F0.wireOp",EDGE,"E43"),sQuery(id+"F0.wireOp",EDGE,"E44"),sQuery(id+"F0.wireOp",EDGE,"E45"),sQuery(id+"F0.wireOp",EDGE,"E46"),sQuery(id+"F0.wireOp",EDGE,"E47"),subQ10,subQ9,subQ8,subQ7,sQuery(id+"F0.wireOp",EDGE,"E52"),sQuery(id+"F0.wireOp",EDGE,"E53"),sQuery(id+"F0.wireOp",EDGE,"E54"),sQuery(id+"F0.wireOp",EDGE,"E55"),subQ6,subQ5,subQ4,subQ3,sQuery(id+"F0.wireOp",EDGE,"E60"),sQuery(id+"F0.wireOp",EDGE,"E61"),sQuery(id+"F0.wireOp",EDGE,"E62"),sQuery(id+"F0.wireOp",EDGE,"E63"),sQuery(id+"F0.wireOp",EDGE,"E64"),subQ2,sQuery(id+"F0.wireOp",EDGE,"E66"),subQ1,sQuery(id+"F0.wireOp",EDGE,"E68"),sQuery(id+"F0.wireOp",EDGE,"E69"),subQ0])],"isStart":false});Q8=makeQuery(id+"F11.opFillet","BLEND_EDGE",EDGE,{"blendedFrom":[makeQuery(id+"F2.boolean.opBoolean","SPLIT",EDGE,{"disambiguationData":[TD([makeQuery(id+"F2.opExtrude","CAP_FACE",FACE,{"disambiguationData":[OSD([sQuery(id+"F0.wireOp",EDGE,"E5.0"),sQuery(id+"F0.wireOp",EDGE,"E5.1"),sQuery(id+"F0.wireOp",EDGE,"E5.2"),sQuery(id+"F0.wireOp",EDGE,"E5.3"),subQ30,subQ29,subQ28,subQ27,subQ26,subQ24,subQ23,subQ22,subQ21,subQ20,subQ19,subQ18,subQ17,subQ16,subQ15,subQ14,subQ13,subQ12,subQ11,subQ10,subQ9,subQ8,subQ7,subQ6,subQ5,subQ4,subQ3,subQ2,subQ1,subQ0])],"isStart":true})])],"derivedFrom":makeQuery(id+"F1.opExtrude","SWEPT_EDGE",EDGE,{"disambiguationData":[OSD([subQ30,subQ24])]})}),subQ33],"blendedInto":[subQ33]});}
            var Q9;
            Q9=makeQuery(id+"F1.opExtrude","CAP_EDGE",EDGE,{"disambiguationData":[OSD([sQuery(id+"F0.wireOp",EDGE,"E11.0")])],"isStart":false});
            var Q10;
            Q10=makeQuery(id+"F1.opExtrude","CAP_EDGE",EDGE,{"disambiguationData":[OSD([sQuery(id+"F0.wireOp",EDGE,"E11.1")])],"isStart":false});
            var Q11;
            {var subQ0=sQuery(id+"F0.wireOp",EDGE,"E70");var subQ1=sQuery(id+"F0.wireOp",EDGE,"E67");var subQ2=sQuery(id+"F0.wireOp",EDGE,"E65");var subQ3=sQuery(id+"F0.wireOp",EDGE,"E59");var subQ4=sQuery(id+"F0.wireOp",EDGE,"E58");var subQ5=sQuery(id+"F0.wireOp",EDGE,"E57");var subQ6=sQuery(id+"F0.wireOp",EDGE,"E56");var subQ7=sQuery(id+"F0.wireOp",EDGE,"E51");var subQ8=sQuery(id+"F0.wireOp",EDGE,"E50");var subQ9=sQuery(id+"F0.wireOp",EDGE,"E49");var subQ10=sQuery(id+"F0.wireOp",EDGE,"E48");var subQ11=sQuery(id+"F0.wireOp",EDGE,"E39");var subQ12=sQuery(id+"F0.wireOp",EDGE,"E38");var subQ13=sQuery(id+"F0.wireOp",EDGE,"E37");var subQ14=sQuery(id+"F0.wireOp",EDGE,"E36");var subQ15=sQuery(id+"F0.wireOp",EDGE,"E35");var subQ16=sQuery(id+"F0.wireOp",EDGE,"E34");var subQ17=sQuery(id+"F0.wireOp",EDGE,"E33");var subQ18=sQuery(id+"F0.wireOp",EDGE,"E32");var subQ19=sQuery(id+"F0.wireOp",EDGE,"E27");var subQ20=sQuery(id+"F0.wireOp",EDGE,"E24");var subQ21=sQuery(id+"F0.wireOp",EDGE,"E22");var subQ22=sQuery(id+"F0.wireOp",EDGE,"E21");var subQ23=sQuery(id+"F0.wireOp",EDGE,"E18");var subQ24=sQuery(id+"F0.wireOp",EDGE,"E15");var subQ25=sQuery(id+"F0.wireOp",EDGE,"E13");var subQ26=sQuery(id+"F0.wireOp",EDGE,"E11.3");var subQ27=sQuery(id+"F0.wireOp",EDGE,"E11.2");var subQ28=sQuery(id+"F0.wireOp",EDGE,"E11.1");var subQ29=sQuery(id+"F0.wireOp",EDGE,"E11.0");var subQ30=makeQuery(id+"F1.opExtrude","CAP_FACE",FACE,{"disambiguationData":[OSD([sQuery(id+"F0.wireOp",EDGE,"E6"),sQuery(id+"F0.wireOp",EDGE,"E7"),sQuery(id+"F0.wireOp",EDGE,"E8"),sQuery(id+"F0.wireOp",EDGE,"E9"),sQuery(id+"F0.wireOp",EDGE,"E10.0"),sQuery(id+"F0.wireOp",EDGE,"E10.1"),sQuery(id+"F0.wireOp",EDGE,"E10.2"),sQuery(id+"F0.wireOp",EDGE,"E10.3"),subQ29,subQ28,subQ27,subQ26,sQuery(id+"F0.wireOp",EDGE,"E12"),subQ25,sQuery(id+"F0.wireOp",EDGE,"E14"),subQ24,subQ23,sQuery(id+"F0.wireOp",EDGE,"E19"),sQuery(id+"F0.wireOp",EDGE,"E20"),subQ22,subQ21,sQuery(id+"F0.wireOp",EDGE,"E23"),subQ20,sQuery(id+"F0.wireOp",EDGE,"E25"),sQuery(id+"F0.wireOp",EDGE,"E26"),subQ19,subQ18,subQ17,subQ16,subQ15,subQ14,subQ13,subQ12,subQ11,sQuery(id+"F0.wireOp",EDGE,"E40"),sQuery(id+"F0.wireOp",EDGE,"E41"),sQuery(id+"F0.wireOp",EDGE,"E42"),sQuery(id+"F0.wireOp",EDGE,"E43"),sQuery(id+"F0.wireOp",EDGE,"E44"),sQuery(id+"F0.wireOp",EDGE,"E45"),sQuery(id+"F0.wireOp",EDGE,"E46"),sQuery(id+"F0.wireOp",EDGE,"E47"),subQ10,subQ9,subQ8,subQ7,sQuery(id+"F0.wireOp",EDGE,"E52"),sQuery(id+"F0.wireOp",EDGE,"E53"),sQuery(id+"F0.wireOp",EDGE,"E54"),sQuery(id+"F0.wireOp",EDGE,"E55"),subQ6,subQ5,subQ4,subQ3,sQuery(id+"F0.wireOp",EDGE,"E60"),sQuery(id+"F0.wireOp",EDGE,"E61"),sQuery(id+"F0.wireOp",EDGE,"E62"),sQuery(id+"F0.wireOp",EDGE,"E63"),sQuery(id+"F0.wireOp",EDGE,"E64"),subQ2,sQuery(id+"F0.wireOp",EDGE,"E66"),subQ1,sQuery(id+"F0.wireOp",EDGE,"E68"),sQuery(id+"F0.wireOp",EDGE,"E69"),subQ0])],"isStart":false});Q11=makeQuery(id+"F11.opFillet","BLEND_EDGE",EDGE,{"blendedFrom":[makeQuery(id+"F2.boolean.opBoolean","SPLIT",EDGE,{"disambiguationData":[TD([makeQuery(id+"F2.opExtrude","CAP_FACE",FACE,{"disambiguationData":[OSD([sQuery(id+"F0.wireOp",EDGE,"E5.0"),sQuery(id+"F0.wireOp",EDGE,"E5.1"),sQuery(id+"F0.wireOp",EDGE,"E5.2"),sQuery(id+"F0.wireOp",EDGE,"E5.3"),subQ29,subQ28,subQ27,subQ26,subQ25,subQ24,subQ23,subQ22,subQ21,subQ20,subQ19,subQ18,subQ17,subQ16,subQ15,subQ14,subQ13,subQ12,subQ11,subQ10,subQ9,subQ8,subQ7,subQ6,subQ5,subQ4,subQ3,subQ2,subQ1,subQ0])],"isStart":true})])],"derivedFrom":makeQuery(id+"F1.opExtrude","SWEPT_EDGE",EDGE,{"disambiguationData":[OSD([subQ28,subQ27])]})}),subQ30],"blendedInto":[subQ30]});}
            var Q12;
            Q12=makeQuery(id+"F1.opExtrude","CAP_EDGE",EDGE,{"disambiguationData":[OSD([sQuery(id+"F0.wireOp",EDGE,"E11.2")])],"isStart":false});
            var Q13;
            Q13=makeQuery(id+"F1.opExtrude","CAP_EDGE",EDGE,{"disambiguationData":[OSD([sQuery(id+"F0.wireOp",EDGE,"E11.3")])],"isStart":false});
            var Q14;
            {var subQ0=sQuery(id+"F0.wireOp",EDGE,"E70");var subQ1=sQuery(id+"F0.wireOp",EDGE,"E67");var subQ2=sQuery(id+"F0.wireOp",EDGE,"E65");var subQ3=sQuery(id+"F0.wireOp",EDGE,"E59");var subQ4=sQuery(id+"F0.wireOp",EDGE,"E58");var subQ5=sQuery(id+"F0.wireOp",EDGE,"E57");var subQ6=sQuery(id+"F0.wireOp",EDGE,"E56");var subQ7=sQuery(id+"F0.wireOp",EDGE,"E51");var subQ8=sQuery(id+"F0.wireOp",EDGE,"E50");var subQ9=sQuery(id+"F0.wireOp",EDGE,"E49");var subQ10=sQuery(id+"F0.wireOp",EDGE,"E48");var subQ11=sQuery(id+"F0.wireOp",EDGE,"E39");var subQ12=sQuery(id+"F0.wireOp",EDGE,"E38");var subQ13=sQuery(id+"F0.wireOp",EDGE,"E37");var subQ14=sQuery(id+"F0.wireOp",EDGE,"E36");var subQ15=sQuery(id+"F0.wireOp",EDGE,"E35");var subQ16=sQuery(id+"F0.wireOp",EDGE,"E34");var subQ17=sQuery(id+"F0.wireOp",EDGE,"E33");var subQ18=sQuery(id+"F0.wireOp",EDGE,"E32");var subQ19=sQuery(id+"F0.wireOp",EDGE,"E27");var subQ20=sQuery(id+"F0.wireOp",EDGE,"E24");var subQ21=sQuery(id+"F0.wireOp",EDGE,"E22");var subQ22=sQuery(id+"F0.wireOp",EDGE,"E21");var subQ23=sQuery(id+"F0.wireOp",EDGE,"E18");var subQ24=sQuery(id+"F0.wireOp",EDGE,"E15");var subQ25=sQuery(id+"F0.wireOp",EDGE,"E13");var subQ26=sQuery(id+"F0.wireOp",EDGE,"E12");var subQ27=sQuery(id+"F0.wireOp",EDGE,"E11.3");var subQ28=sQuery(id+"F0.wireOp",EDGE,"E11.2");var subQ29=sQuery(id+"F0.wireOp",EDGE,"E11.1");var subQ30=sQuery(id+"F0.wireOp",EDGE,"E11.0");var subQ31=sQuery(id+"F0.wireOp",EDGE,"E7");var subQ32=sQuery(id+"F0.wireOp",EDGE,"E6");var subQ33=makeQuery(id+"F1.opExtrude","CAP_FACE",FACE,{"disambiguationData":[OSD([subQ32,subQ31,sQuery(id+"F0.wireOp",EDGE,"E8"),sQuery(id+"F0.wireOp",EDGE,"E9"),sQuery(id+"F0.wireOp",EDGE,"E10.0"),sQuery(id+"F0.wireOp",EDGE,"E10.1"),sQuery(id+"F0.wireOp",EDGE,"E10.2"),sQuery(id+"F0.wireOp",EDGE,"E10.3"),subQ30,subQ29,subQ28,subQ27,subQ26,subQ25,sQuery(id+"F0.wireOp",EDGE,"E14"),subQ24,subQ23,sQuery(id+"F0.wireOp",EDGE,"E19"),sQuery(id+"F0.wireOp",EDGE,"E20"),subQ22,subQ21,sQuery(id+"F0.wireOp",EDGE,"E23"),subQ20,sQuery(id+"F0.wireOp",EDGE,"E25"),sQuery(id+"F0.wireOp",EDGE,"E26"),subQ19,subQ18,subQ17,subQ16,subQ15,subQ14,subQ13,subQ12,subQ11,sQuery(id+"F0.wireOp",EDGE,"E40"),sQuery(id+"F0.wireOp",EDGE,"E41"),sQuery(id+"F0.wireOp",EDGE,"E42"),sQuery(id+"F0.wireOp",EDGE,"E43"),sQuery(id+"F0.wireOp",EDGE,"E44"),sQuery(id+"F0.wireOp",EDGE,"E45"),sQuery(id+"F0.wireOp",EDGE,"E46"),sQuery(id+"F0.wireOp",EDGE,"E47"),subQ10,subQ9,subQ8,subQ7,sQuery(id+"F0.wireOp",EDGE,"E52"),sQuery(id+"F0.wireOp",EDGE,"E53"),sQuery(id+"F0.wireOp",EDGE,"E54"),sQuery(id+"F0.wireOp",EDGE,"E55"),subQ6,subQ5,subQ4,subQ3,sQuery(id+"F0.wireOp",EDGE,"E60"),sQuery(id+"F0.wireOp",EDGE,"E61"),sQuery(id+"F0.wireOp",EDGE,"E62"),sQuery(id+"F0.wireOp",EDGE,"E63"),sQuery(id+"F0.wireOp",EDGE,"E64"),subQ2,sQuery(id+"F0.wireOp",EDGE,"E66"),subQ1,sQuery(id+"F0.wireOp",EDGE,"E68"),sQuery(id+"F0.wireOp",EDGE,"E69"),subQ0])],"isStart":false});Q14=makeQuery(id+"F11.opFillet","BLEND_EDGE",EDGE,{"blendedFrom":[makeQuery(id+"F2.boolean.opBoolean","SPLIT",EDGE,{"disambiguationData":[TD([makeQuery(id+"F2.opExtrude","CAP_FACE",FACE,{"disambiguationData":[OSD([sQuery(id+"F0.wireOp",EDGE,"E5.0"),sQuery(id+"F0.wireOp",EDGE,"E5.1"),sQuery(id+"F0.wireOp",EDGE,"E5.2"),sQuery(id+"F0.wireOp",EDGE,"E5.3"),subQ30,subQ29,subQ28,subQ27,subQ25,subQ24,subQ23,subQ22,subQ21,subQ20,subQ19,subQ18,subQ17,subQ16,subQ15,subQ14,subQ13,subQ12,subQ11,subQ10,subQ9,subQ8,subQ7,subQ6,subQ5,subQ4,subQ3,subQ2,subQ1,subQ0])],"isStart":true})])],"derivedFrom":makeQuery(id+"F1.opExtrude","SWEPT_EDGE",EDGE,{"disambiguationData":[OSD([subQ27,subQ25])]})}),subQ33],"blendedInto":[subQ33]});}
            var Q15;
            Q15=makeQuery(id+"F1.opExtrude","CAP_EDGE",EDGE,{"disambiguationData":[OSD([sQuery(id+"F0.wireOp",EDGE,"E6"),sQuery(id+"F0.wireOp",EDGE,"E7"),sQuery(id+"F0.wireOp",EDGE,"E12"),sQuery(id+"F0.wireOp",EDGE,"E13")])],"isStart":false});
            var Q16;
            {var subQ0=sQuery(id+"F0.wireOp",EDGE,"E69");var subQ1=sQuery(id+"F0.wireOp",EDGE,"E68");var subQ2=sQuery(id+"F0.wireOp",EDGE,"E66");var subQ3=sQuery(id+"F0.wireOp",EDGE,"E64");var subQ4=sQuery(id+"F0.wireOp",EDGE,"E63");var subQ5=sQuery(id+"F0.wireOp",EDGE,"E62");var subQ6=sQuery(id+"F0.wireOp",EDGE,"E61");var subQ7=sQuery(id+"F0.wireOp",EDGE,"E60");var subQ8=sQuery(id+"F0.wireOp",EDGE,"E55");var subQ9=sQuery(id+"F0.wireOp",EDGE,"E54");var subQ10=sQuery(id+"F0.wireOp",EDGE,"E53");var subQ11=sQuery(id+"F0.wireOp",EDGE,"E52");var subQ12=sQuery(id+"F0.wireOp",EDGE,"E47");var subQ13=sQuery(id+"F0.wireOp",EDGE,"E46");var subQ14=sQuery(id+"F0.wireOp",EDGE,"E45");var subQ15=sQuery(id+"F0.wireOp",EDGE,"E44");var subQ16=sQuery(id+"F0.wireOp",EDGE,"E43");var subQ17=sQuery(id+"F0.wireOp",EDGE,"E42");var subQ18=sQuery(id+"F0.wireOp",EDGE,"E41");var subQ19=sQuery(id+"F0.wireOp",EDGE,"E40");var subQ20=sQuery(id+"F0.wireOp",EDGE,"E26");var subQ21=sQuery(id+"F0.wireOp",EDGE,"E25");var subQ22=sQuery(id+"F0.wireOp",EDGE,"E23");var subQ23=sQuery(id+"F0.wireOp",EDGE,"E20");var subQ24=sQuery(id+"F0.wireOp",EDGE,"E19");var subQ25=sQuery(id+"F0.wireOp",EDGE,"E14");var subQ26=sQuery(id+"F0.wireOp",EDGE,"E13");var subQ27=sQuery(id+"F0.wireOp",EDGE,"E12");var subQ28=sQuery(id+"F0.wireOp",EDGE,"E10.3");var subQ29=sQuery(id+"F0.wireOp",EDGE,"E10.2");var subQ30=sQuery(id+"F0.wireOp",EDGE,"E10.1");var subQ31=sQuery(id+"F0.wireOp",EDGE,"E10.0");var subQ32=sQuery(id+"F0.wireOp",EDGE,"E7");var subQ33=sQuery(id+"F0.wireOp",EDGE,"E6");var subQ34=makeQuery(id+"F1.opExtrude","CAP_FACE",FACE,{"disambiguationData":[OSD([subQ33,subQ32,sQuery(id+"F0.wireOp",EDGE,"E8"),sQuery(id+"F0.wireOp",EDGE,"E9"),subQ31,subQ30,subQ29,subQ28,sQuery(id+"F0.wireOp",EDGE,"E11.0"),sQuery(id+"F0.wireOp",EDGE,"E11.1"),sQuery(id+"F0.wireOp",EDGE,"E11.2"),sQuery(id+"F0.wireOp",EDGE,"E11.3"),subQ27,subQ26,subQ25,sQuery(id+"F0.wireOp",EDGE,"E15"),sQuery(id+"F0.wireOp",EDGE,"E18"),subQ24,subQ23,sQuery(id+"F0.wireOp",EDGE,"E21"),sQuery(id+"F0.wireOp",EDGE,"E22"),subQ22,sQuery(id+"F0.wireOp",EDGE,"E24"),subQ21,subQ20,sQuery(id+"F0.wireOp",EDGE,"E27"),sQuery(id+"F0.wireOp",EDGE,"E32"),sQuery(id+"F0.wireOp",EDGE,"E33"),sQuery(id+"F0.wireOp",EDGE,"E34"),sQuery(id+"F0.wireOp",EDGE,"E35"),sQuery(id+"F0.wireOp",EDGE,"E36"),sQuery(id+"F0.wireOp",EDGE,"E37"),sQuery(id+"F0.wireOp",EDGE,"E38"),sQuery(id+"F0.wireOp",EDGE,"E39"),subQ19,subQ18,subQ17,subQ16,subQ15,subQ14,subQ13,subQ12,sQuery(id+"F0.wireOp",EDGE,"E48"),sQuery(id+"F0.wireOp",EDGE,"E49"),sQuery(id+"F0.wireOp",EDGE,"E50"),sQuery(id+"F0.wireOp",EDGE,"E51"),subQ11,subQ10,subQ9,subQ8,sQuery(id+"F0.wireOp",EDGE,"E56"),sQuery(id+"F0.wireOp",EDGE,"E57"),sQuery(id+"F0.wireOp",EDGE,"E58"),sQuery(id+"F0.wireOp",EDGE,"E59"),subQ7,subQ6,subQ5,subQ4,subQ3,sQuery(id+"F0.wireOp",EDGE,"E65"),subQ2,sQuery(id+"F0.wireOp",EDGE,"E67"),subQ1,subQ0,sQuery(id+"F0.wireOp",EDGE,"E70")])],"isStart":false});Q16=makeQuery(id+"F11.opFillet","BLEND_EDGE",EDGE,{"blendedFrom":[makeQuery(id+"F2.boolean.opBoolean","SPLIT",EDGE,{"disambiguationData":[TD([makeQuery(id+"F2.opExtrude","CAP_FACE",FACE,{"disambiguationData":[OSD([sQuery(id+"F0.wireOp",EDGE,"E4.0"),sQuery(id+"F0.wireOp",EDGE,"E4.1"),sQuery(id+"F0.wireOp",EDGE,"E4.2"),sQuery(id+"F0.wireOp",EDGE,"E4.3"),subQ31,subQ30,subQ29,subQ28,subQ27,subQ25,subQ24,subQ23,subQ22,subQ21,subQ20,subQ19,subQ18,subQ17,subQ16,subQ15,subQ14,subQ13,subQ12,subQ11,subQ10,subQ9,subQ8,subQ7,subQ6,subQ5,subQ4,subQ3,subQ2,subQ1,subQ0])],"isStart":true})])],"derivedFrom":makeQuery(id+"F1.opExtrude","SWEPT_EDGE",EDGE,{"disambiguationData":[OSD([subQ28,subQ27])]})}),subQ34],"blendedInto":[subQ34]});}
            var Q17;
            Q17=makeQuery(id+"F1.opExtrude","CAP_EDGE",EDGE,{"disambiguationData":[OSD([sQuery(id+"F0.wireOp",EDGE,"E8"),sQuery(id+"F0.wireOp",EDGE,"E9"),sQuery(id+"F0.wireOp",EDGE,"E14"),sQuery(id+"F0.wireOp",EDGE,"E15")])],"isStart":true});
            var Q18;
            {var subQ0=sQuery(id+"F0.wireOp",EDGE,"E70");var subQ1=sQuery(id+"F0.wireOp",EDGE,"E67");var subQ2=sQuery(id+"F0.wireOp",EDGE,"E65");var subQ3=sQuery(id+"F0.wireOp",EDGE,"E59");var subQ4=sQuery(id+"F0.wireOp",EDGE,"E58");var subQ5=sQuery(id+"F0.wireOp",EDGE,"E57");var subQ6=sQuery(id+"F0.wireOp",EDGE,"E56");var subQ7=sQuery(id+"F0.wireOp",EDGE,"E51");var subQ8=sQuery(id+"F0.wireOp",EDGE,"E50");var subQ9=sQuery(id+"F0.wireOp",EDGE,"E49");var subQ10=sQuery(id+"F0.wireOp",EDGE,"E48");var subQ11=sQuery(id+"F0.wireOp",EDGE,"E39");var subQ12=sQuery(id+"F0.wireOp",EDGE,"E38");var subQ13=sQuery(id+"F0.wireOp",EDGE,"E37");var subQ14=sQuery(id+"F0.wireOp",EDGE,"E36");var subQ15=sQuery(id+"F0.wireOp",EDGE,"E35");var subQ16=sQuery(id+"F0.wireOp",EDGE,"E34");var subQ17=sQuery(id+"F0.wireOp",EDGE,"E33");var subQ18=sQuery(id+"F0.wireOp",EDGE,"E32");var subQ19=sQuery(id+"F0.wireOp",EDGE,"E27");var subQ20=sQuery(id+"F0.wireOp",EDGE,"E24");var subQ21=sQuery(id+"F0.wireOp",EDGE,"E22");var subQ22=sQuery(id+"F0.wireOp",EDGE,"E21");var subQ23=sQuery(id+"F0.wireOp",EDGE,"E18");var subQ24=sQuery(id+"F0.wireOp",EDGE,"E15");var subQ25=sQuery(id+"F0.wireOp",EDGE,"E14");var subQ26=sQuery(id+"F0.wireOp",EDGE,"E13");var subQ27=sQuery(id+"F0.wireOp",EDGE,"E11.3");var subQ28=sQuery(id+"F0.wireOp",EDGE,"E11.2");var subQ29=sQuery(id+"F0.wireOp",EDGE,"E11.1");var subQ30=sQuery(id+"F0.wireOp",EDGE,"E11.0");var subQ31=sQuery(id+"F0.wireOp",EDGE,"E9");var subQ32=sQuery(id+"F0.wireOp",EDGE,"E8");var subQ33=makeQuery(id+"F1.opExtrude","CAP_FACE",FACE,{"disambiguationData":[OSD([sQuery(id+"F0.wireOp",EDGE,"E6"),sQuery(id+"F0.wireOp",EDGE,"E7"),subQ32,subQ31,sQuery(id+"F0.wireOp",EDGE,"E10.0"),sQuery(id+"F0.wireOp",EDGE,"E10.1"),sQuery(id+"F0.wireOp",EDGE,"E10.2"),sQuery(id+"F0.wireOp",EDGE,"E10.3"),subQ30,subQ29,subQ28,subQ27,sQuery(id+"F0.wireOp",EDGE,"E12"),subQ26,subQ25,subQ24,subQ23,sQuery(id+"F0.wireOp",EDGE,"E19"),sQuery(id+"F0.wireOp",EDGE,"E20"),subQ22,subQ21,sQuery(id+"F0.wireOp",EDGE,"E23"),subQ20,sQuery(id+"F0.wireOp",EDGE,"E25"),sQuery(id+"F0.wireOp",EDGE,"E26"),subQ19,subQ18,subQ17,subQ16,subQ15,subQ14,subQ13,subQ12,subQ11,sQuery(id+"F0.wireOp",EDGE,"E40"),sQuery(id+"F0.wireOp",EDGE,"E41"),sQuery(id+"F0.wireOp",EDGE,"E42"),sQuery(id+"F0.wireOp",EDGE,"E43"),sQuery(id+"F0.wireOp",EDGE,"E44"),sQuery(id+"F0.wireOp",EDGE,"E45"),sQuery(id+"F0.wireOp",EDGE,"E46"),sQuery(id+"F0.wireOp",EDGE,"E47"),subQ10,subQ9,subQ8,subQ7,sQuery(id+"F0.wireOp",EDGE,"E52"),sQuery(id+"F0.wireOp",EDGE,"E53"),sQuery(id+"F0.wireOp",EDGE,"E54"),sQuery(id+"F0.wireOp",EDGE,"E55"),subQ6,subQ5,subQ4,subQ3,sQuery(id+"F0.wireOp",EDGE,"E60"),sQuery(id+"F0.wireOp",EDGE,"E61"),sQuery(id+"F0.wireOp",EDGE,"E62"),sQuery(id+"F0.wireOp",EDGE,"E63"),sQuery(id+"F0.wireOp",EDGE,"E64"),subQ2,sQuery(id+"F0.wireOp",EDGE,"E66"),subQ1,sQuery(id+"F0.wireOp",EDGE,"E68"),sQuery(id+"F0.wireOp",EDGE,"E69"),subQ0])],"isStart":true});Q18=makeQuery(id+"F11.opFillet","BLEND_EDGE",EDGE,{"blendedFrom":[makeQuery(id+"F2.boolean.opBoolean","SPLIT",EDGE,{"disambiguationData":[TD([makeQuery(id+"F2.opExtrude","CAP_FACE",FACE,{"disambiguationData":[OSD([sQuery(id+"F0.wireOp",EDGE,"E5.0"),sQuery(id+"F0.wireOp",EDGE,"E5.1"),sQuery(id+"F0.wireOp",EDGE,"E5.2"),sQuery(id+"F0.wireOp",EDGE,"E5.3"),subQ30,subQ29,subQ28,subQ27,subQ26,subQ24,subQ23,subQ22,subQ21,subQ20,subQ19,subQ18,subQ17,subQ16,subQ15,subQ14,subQ13,subQ12,subQ11,subQ10,subQ9,subQ8,subQ7,subQ6,subQ5,subQ4,subQ3,subQ2,subQ1,subQ0])],"isStart":false})])],"derivedFrom":makeQuery(id+"F1.opExtrude","SWEPT_EDGE",EDGE,{"disambiguationData":[OSD([subQ30,subQ24])]})}),subQ33],"blendedInto":[subQ33]});}
            var Q19;
            Q19=makeQuery(id+"F1.opExtrude","CAP_EDGE",EDGE,{"disambiguationData":[OSD([sQuery(id+"F0.wireOp",EDGE,"E11.0")])],"isStart":true});
            var Q20;
            Q20=makeQuery(id+"F1.opExtrude","CAP_EDGE",EDGE,{"disambiguationData":[OSD([sQuery(id+"F0.wireOp",EDGE,"E11.1")])],"isStart":true});
            var Q21;
            {var subQ0=sQuery(id+"F0.wireOp",EDGE,"E70");var subQ1=sQuery(id+"F0.wireOp",EDGE,"E67");var subQ2=sQuery(id+"F0.wireOp",EDGE,"E65");var subQ3=sQuery(id+"F0.wireOp",EDGE,"E59");var subQ4=sQuery(id+"F0.wireOp",EDGE,"E58");var subQ5=sQuery(id+"F0.wireOp",EDGE,"E57");var subQ6=sQuery(id+"F0.wireOp",EDGE,"E56");var subQ7=sQuery(id+"F0.wireOp",EDGE,"E51");var subQ8=sQuery(id+"F0.wireOp",EDGE,"E50");var subQ9=sQuery(id+"F0.wireOp",EDGE,"E49");var subQ10=sQuery(id+"F0.wireOp",EDGE,"E48");var subQ11=sQuery(id+"F0.wireOp",EDGE,"E39");var subQ12=sQuery(id+"F0.wireOp",EDGE,"E38");var subQ13=sQuery(id+"F0.wireOp",EDGE,"E37");var subQ14=sQuery(id+"F0.wireOp",EDGE,"E36");var subQ15=sQuery(id+"F0.wireOp",EDGE,"E35");var subQ16=sQuery(id+"F0.wireOp",EDGE,"E34");var subQ17=sQuery(id+"F0.wireOp",EDGE,"E33");var subQ18=sQuery(id+"F0.wireOp",EDGE,"E32");var subQ19=sQuery(id+"F0.wireOp",EDGE,"E27");var subQ20=sQuery(id+"F0.wireOp",EDGE,"E24");var subQ21=sQuery(id+"F0.wireOp",EDGE,"E22");var subQ22=sQuery(id+"F0.wireOp",EDGE,"E21");var subQ23=sQuery(id+"F0.wireOp",EDGE,"E18");var subQ24=sQuery(id+"F0.wireOp",EDGE,"E15");var subQ25=sQuery(id+"F0.wireOp",EDGE,"E13");var subQ26=sQuery(id+"F0.wireOp",EDGE,"E11.3");var subQ27=sQuery(id+"F0.wireOp",EDGE,"E11.2");var subQ28=sQuery(id+"F0.wireOp",EDGE,"E11.1");var subQ29=sQuery(id+"F0.wireOp",EDGE,"E11.0");var subQ30=makeQuery(id+"F1.opExtrude","CAP_FACE",FACE,{"disambiguationData":[OSD([sQuery(id+"F0.wireOp",EDGE,"E6"),sQuery(id+"F0.wireOp",EDGE,"E7"),sQuery(id+"F0.wireOp",EDGE,"E8"),sQuery(id+"F0.wireOp",EDGE,"E9"),sQuery(id+"F0.wireOp",EDGE,"E10.0"),sQuery(id+"F0.wireOp",EDGE,"E10.1"),sQuery(id+"F0.wireOp",EDGE,"E10.2"),sQuery(id+"F0.wireOp",EDGE,"E10.3"),subQ29,subQ28,subQ27,subQ26,sQuery(id+"F0.wireOp",EDGE,"E12"),subQ25,sQuery(id+"F0.wireOp",EDGE,"E14"),subQ24,subQ23,sQuery(id+"F0.wireOp",EDGE,"E19"),sQuery(id+"F0.wireOp",EDGE,"E20"),subQ22,subQ21,sQuery(id+"F0.wireOp",EDGE,"E23"),subQ20,sQuery(id+"F0.wireOp",EDGE,"E25"),sQuery(id+"F0.wireOp",EDGE,"E26"),subQ19,subQ18,subQ17,subQ16,subQ15,subQ14,subQ13,subQ12,subQ11,sQuery(id+"F0.wireOp",EDGE,"E40"),sQuery(id+"F0.wireOp",EDGE,"E41"),sQuery(id+"F0.wireOp",EDGE,"E42"),sQuery(id+"F0.wireOp",EDGE,"E43"),sQuery(id+"F0.wireOp",EDGE,"E44"),sQuery(id+"F0.wireOp",EDGE,"E45"),sQuery(id+"F0.wireOp",EDGE,"E46"),sQuery(id+"F0.wireOp",EDGE,"E47"),subQ10,subQ9,subQ8,subQ7,sQuery(id+"F0.wireOp",EDGE,"E52"),sQuery(id+"F0.wireOp",EDGE,"E53"),sQuery(id+"F0.wireOp",EDGE,"E54"),sQuery(id+"F0.wireOp",EDGE,"E55"),subQ6,subQ5,subQ4,subQ3,sQuery(id+"F0.wireOp",EDGE,"E60"),sQuery(id+"F0.wireOp",EDGE,"E61"),sQuery(id+"F0.wireOp",EDGE,"E62"),sQuery(id+"F0.wireOp",EDGE,"E63"),sQuery(id+"F0.wireOp",EDGE,"E64"),subQ2,sQuery(id+"F0.wireOp",EDGE,"E66"),subQ1,sQuery(id+"F0.wireOp",EDGE,"E68"),sQuery(id+"F0.wireOp",EDGE,"E69"),subQ0])],"isStart":true});Q21=makeQuery(id+"F11.opFillet","BLEND_EDGE",EDGE,{"blendedFrom":[makeQuery(id+"F2.boolean.opBoolean","SPLIT",EDGE,{"disambiguationData":[TD([makeQuery(id+"F2.opExtrude","CAP_FACE",FACE,{"disambiguationData":[OSD([sQuery(id+"F0.wireOp",EDGE,"E5.0"),sQuery(id+"F0.wireOp",EDGE,"E5.1"),sQuery(id+"F0.wireOp",EDGE,"E5.2"),sQuery(id+"F0.wireOp",EDGE,"E5.3"),subQ29,subQ28,subQ27,subQ26,subQ25,subQ24,subQ23,subQ22,subQ21,subQ20,subQ19,subQ18,subQ17,subQ16,subQ15,subQ14,subQ13,subQ12,subQ11,subQ10,subQ9,subQ8,subQ7,subQ6,subQ5,subQ4,subQ3,subQ2,subQ1,subQ0])],"isStart":false})])],"derivedFrom":makeQuery(id+"F1.opExtrude","SWEPT_EDGE",EDGE,{"disambiguationData":[OSD([subQ28,subQ27])]})}),subQ30],"blendedInto":[subQ30]});}
            var Q22;
            Q22=makeQuery(id+"F1.opExtrude","CAP_EDGE",EDGE,{"disambiguationData":[OSD([sQuery(id+"F0.wireOp",EDGE,"E11.2")])],"isStart":true});
            var Q23;
            Q23=makeQuery(id+"F1.opExtrude","CAP_EDGE",EDGE,{"disambiguationData":[OSD([sQuery(id+"F0.wireOp",EDGE,"E11.3")])],"isStart":true});
            var Q24;
            {var subQ0=sQuery(id+"F0.wireOp",EDGE,"E70");var subQ1=sQuery(id+"F0.wireOp",EDGE,"E67");var subQ2=sQuery(id+"F0.wireOp",EDGE,"E65");var subQ3=sQuery(id+"F0.wireOp",EDGE,"E59");var subQ4=sQuery(id+"F0.wireOp",EDGE,"E58");var subQ5=sQuery(id+"F0.wireOp",EDGE,"E57");var subQ6=sQuery(id+"F0.wireOp",EDGE,"E56");var subQ7=sQuery(id+"F0.wireOp",EDGE,"E51");var subQ8=sQuery(id+"F0.wireOp",EDGE,"E50");var subQ9=sQuery(id+"F0.wireOp",EDGE,"E49");var subQ10=sQuery(id+"F0.wireOp",EDGE,"E48");var subQ11=sQuery(id+"F0.wireOp",EDGE,"E39");var subQ12=sQuery(id+"F0.wireOp",EDGE,"E38");var subQ13=sQuery(id+"F0.wireOp",EDGE,"E37");var subQ14=sQuery(id+"F0.wireOp",EDGE,"E36");var subQ15=sQuery(id+"F0.wireOp",EDGE,"E35");var subQ16=sQuery(id+"F0.wireOp",EDGE,"E34");var subQ17=sQuery(id+"F0.wireOp",EDGE,"E33");var subQ18=sQuery(id+"F0.wireOp",EDGE,"E32");var subQ19=sQuery(id+"F0.wireOp",EDGE,"E27");var subQ20=sQuery(id+"F0.wireOp",EDGE,"E24");var subQ21=sQuery(id+"F0.wireOp",EDGE,"E22");var subQ22=sQuery(id+"F0.wireOp",EDGE,"E21");var subQ23=sQuery(id+"F0.wireOp",EDGE,"E18");var subQ24=sQuery(id+"F0.wireOp",EDGE,"E15");var subQ25=sQuery(id+"F0.wireOp",EDGE,"E13");var subQ26=sQuery(id+"F0.wireOp",EDGE,"E12");var subQ27=sQuery(id+"F0.wireOp",EDGE,"E11.3");var subQ28=sQuery(id+"F0.wireOp",EDGE,"E11.2");var subQ29=sQuery(id+"F0.wireOp",EDGE,"E11.1");var subQ30=sQuery(id+"F0.wireOp",EDGE,"E11.0");var subQ31=sQuery(id+"F0.wireOp",EDGE,"E7");var subQ32=sQuery(id+"F0.wireOp",EDGE,"E6");var subQ33=makeQuery(id+"F1.opExtrude","CAP_FACE",FACE,{"disambiguationData":[OSD([subQ32,subQ31,sQuery(id+"F0.wireOp",EDGE,"E8"),sQuery(id+"F0.wireOp",EDGE,"E9"),sQuery(id+"F0.wireOp",EDGE,"E10.0"),sQuery(id+"F0.wireOp",EDGE,"E10.1"),sQuery(id+"F0.wireOp",EDGE,"E10.2"),sQuery(id+"F0.wireOp",EDGE,"E10.3"),subQ30,subQ29,subQ28,subQ27,subQ26,subQ25,sQuery(id+"F0.wireOp",EDGE,"E14"),subQ24,subQ23,sQuery(id+"F0.wireOp",EDGE,"E19"),sQuery(id+"F0.wireOp",EDGE,"E20"),subQ22,subQ21,sQuery(id+"F0.wireOp",EDGE,"E23"),subQ20,sQuery(id+"F0.wireOp",EDGE,"E25"),sQuery(id+"F0.wireOp",EDGE,"E26"),subQ19,subQ18,subQ17,subQ16,subQ15,subQ14,subQ13,subQ12,subQ11,sQuery(id+"F0.wireOp",EDGE,"E40"),sQuery(id+"F0.wireOp",EDGE,"E41"),sQuery(id+"F0.wireOp",EDGE,"E42"),sQuery(id+"F0.wireOp",EDGE,"E43"),sQuery(id+"F0.wireOp",EDGE,"E44"),sQuery(id+"F0.wireOp",EDGE,"E45"),sQuery(id+"F0.wireOp",EDGE,"E46"),sQuery(id+"F0.wireOp",EDGE,"E47"),subQ10,subQ9,subQ8,subQ7,sQuery(id+"F0.wireOp",EDGE,"E52"),sQuery(id+"F0.wireOp",EDGE,"E53"),sQuery(id+"F0.wireOp",EDGE,"E54"),sQuery(id+"F0.wireOp",EDGE,"E55"),subQ6,subQ5,subQ4,subQ3,sQuery(id+"F0.wireOp",EDGE,"E60"),sQuery(id+"F0.wireOp",EDGE,"E61"),sQuery(id+"F0.wireOp",EDGE,"E62"),sQuery(id+"F0.wireOp",EDGE,"E63"),sQuery(id+"F0.wireOp",EDGE,"E64"),subQ2,sQuery(id+"F0.wireOp",EDGE,"E66"),subQ1,sQuery(id+"F0.wireOp",EDGE,"E68"),sQuery(id+"F0.wireOp",EDGE,"E69"),subQ0])],"isStart":true});Q24=makeQuery(id+"F11.opFillet","BLEND_EDGE",EDGE,{"blendedFrom":[makeQuery(id+"F2.boolean.opBoolean","SPLIT",EDGE,{"disambiguationData":[TD([makeQuery(id+"F2.opExtrude","CAP_FACE",FACE,{"disambiguationData":[OSD([sQuery(id+"F0.wireOp",EDGE,"E5.0"),sQuery(id+"F0.wireOp",EDGE,"E5.1"),sQuery(id+"F0.wireOp",EDGE,"E5.2"),sQuery(id+"F0.wireOp",EDGE,"E5.3"),subQ30,subQ29,subQ28,subQ27,subQ25,subQ24,subQ23,subQ22,subQ21,subQ20,subQ19,subQ18,subQ17,subQ16,subQ15,subQ14,subQ13,subQ12,subQ11,subQ10,subQ9,subQ8,subQ7,subQ6,subQ5,subQ4,subQ3,subQ2,subQ1,subQ0])],"isStart":false})])],"derivedFrom":makeQuery(id+"F1.opExtrude","SWEPT_EDGE",EDGE,{"disambiguationData":[OSD([subQ27,subQ25])]})}),subQ33],"blendedInto":[subQ33]});}
            var Q25;
            Q25=makeQuery(id+"F1.opExtrude","CAP_EDGE",EDGE,{"disambiguationData":[OSD([sQuery(id+"F0.wireOp",EDGE,"E6"),sQuery(id+"F0.wireOp",EDGE,"E7"),sQuery(id+"F0.wireOp",EDGE,"E12"),sQuery(id+"F0.wireOp",EDGE,"E13")])],"isStart":true});
            var Q26;
            {var subQ0=sQuery(id+"F0.wireOp",EDGE,"E69");var subQ1=sQuery(id+"F0.wireOp",EDGE,"E68");var subQ2=sQuery(id+"F0.wireOp",EDGE,"E66");var subQ3=sQuery(id+"F0.wireOp",EDGE,"E64");var subQ4=sQuery(id+"F0.wireOp",EDGE,"E63");var subQ5=sQuery(id+"F0.wireOp",EDGE,"E62");var subQ6=sQuery(id+"F0.wireOp",EDGE,"E61");var subQ7=sQuery(id+"F0.wireOp",EDGE,"E60");var subQ8=sQuery(id+"F0.wireOp",EDGE,"E55");var subQ9=sQuery(id+"F0.wireOp",EDGE,"E54");var subQ10=sQuery(id+"F0.wireOp",EDGE,"E53");var subQ11=sQuery(id+"F0.wireOp",EDGE,"E52");var subQ12=sQuery(id+"F0.wireOp",EDGE,"E47");var subQ13=sQuery(id+"F0.wireOp",EDGE,"E46");var subQ14=sQuery(id+"F0.wireOp",EDGE,"E45");var subQ15=sQuery(id+"F0.wireOp",EDGE,"E44");var subQ16=sQuery(id+"F0.wireOp",EDGE,"E43");var subQ17=sQuery(id+"F0.wireOp",EDGE,"E42");var subQ18=sQuery(id+"F0.wireOp",EDGE,"E41");var subQ19=sQuery(id+"F0.wireOp",EDGE,"E40");var subQ20=sQuery(id+"F0.wireOp",EDGE,"E26");var subQ21=sQuery(id+"F0.wireOp",EDGE,"E25");var subQ22=sQuery(id+"F0.wireOp",EDGE,"E23");var subQ23=sQuery(id+"F0.wireOp",EDGE,"E20");var subQ24=sQuery(id+"F0.wireOp",EDGE,"E19");var subQ25=sQuery(id+"F0.wireOp",EDGE,"E14");var subQ26=sQuery(id+"F0.wireOp",EDGE,"E13");var subQ27=sQuery(id+"F0.wireOp",EDGE,"E12");var subQ28=sQuery(id+"F0.wireOp",EDGE,"E10.3");var subQ29=sQuery(id+"F0.wireOp",EDGE,"E10.2");var subQ30=sQuery(id+"F0.wireOp",EDGE,"E10.1");var subQ31=sQuery(id+"F0.wireOp",EDGE,"E10.0");var subQ32=sQuery(id+"F0.wireOp",EDGE,"E7");var subQ33=sQuery(id+"F0.wireOp",EDGE,"E6");var subQ34=makeQuery(id+"F1.opExtrude","CAP_FACE",FACE,{"disambiguationData":[OSD([subQ33,subQ32,sQuery(id+"F0.wireOp",EDGE,"E8"),sQuery(id+"F0.wireOp",EDGE,"E9"),subQ31,subQ30,subQ29,subQ28,sQuery(id+"F0.wireOp",EDGE,"E11.0"),sQuery(id+"F0.wireOp",EDGE,"E11.1"),sQuery(id+"F0.wireOp",EDGE,"E11.2"),sQuery(id+"F0.wireOp",EDGE,"E11.3"),subQ27,subQ26,subQ25,sQuery(id+"F0.wireOp",EDGE,"E15"),sQuery(id+"F0.wireOp",EDGE,"E18"),subQ24,subQ23,sQuery(id+"F0.wireOp",EDGE,"E21"),sQuery(id+"F0.wireOp",EDGE,"E22"),subQ22,sQuery(id+"F0.wireOp",EDGE,"E24"),subQ21,subQ20,sQuery(id+"F0.wireOp",EDGE,"E27"),sQuery(id+"F0.wireOp",EDGE,"E32"),sQuery(id+"F0.wireOp",EDGE,"E33"),sQuery(id+"F0.wireOp",EDGE,"E34"),sQuery(id+"F0.wireOp",EDGE,"E35"),sQuery(id+"F0.wireOp",EDGE,"E36"),sQuery(id+"F0.wireOp",EDGE,"E37"),sQuery(id+"F0.wireOp",EDGE,"E38"),sQuery(id+"F0.wireOp",EDGE,"E39"),subQ19,subQ18,subQ17,subQ16,subQ15,subQ14,subQ13,subQ12,sQuery(id+"F0.wireOp",EDGE,"E48"),sQuery(id+"F0.wireOp",EDGE,"E49"),sQuery(id+"F0.wireOp",EDGE,"E50"),sQuery(id+"F0.wireOp",EDGE,"E51"),subQ11,subQ10,subQ9,subQ8,sQuery(id+"F0.wireOp",EDGE,"E56"),sQuery(id+"F0.wireOp",EDGE,"E57"),sQuery(id+"F0.wireOp",EDGE,"E58"),sQuery(id+"F0.wireOp",EDGE,"E59"),subQ7,subQ6,subQ5,subQ4,subQ3,sQuery(id+"F0.wireOp",EDGE,"E65"),subQ2,sQuery(id+"F0.wireOp",EDGE,"E67"),subQ1,subQ0,sQuery(id+"F0.wireOp",EDGE,"E70")])],"isStart":true});Q26=makeQuery(id+"F11.opFillet","BLEND_EDGE",EDGE,{"blendedFrom":[makeQuery(id+"F2.boolean.opBoolean","SPLIT",EDGE,{"disambiguationData":[TD([makeQuery(id+"F2.opExtrude","CAP_FACE",FACE,{"disambiguationData":[OSD([sQuery(id+"F0.wireOp",EDGE,"E4.0"),sQuery(id+"F0.wireOp",EDGE,"E4.1"),sQuery(id+"F0.wireOp",EDGE,"E4.2"),sQuery(id+"F0.wireOp",EDGE,"E4.3"),subQ31,subQ30,subQ29,subQ28,subQ27,subQ25,subQ24,subQ23,subQ22,subQ21,subQ20,subQ19,subQ18,subQ17,subQ16,subQ15,subQ14,subQ13,subQ12,subQ11,subQ10,subQ9,subQ8,subQ7,subQ6,subQ5,subQ4,subQ3,subQ2,subQ1,subQ0])],"isStart":false})])],"derivedFrom":makeQuery(id+"F1.opExtrude","SWEPT_EDGE",EDGE,{"disambiguationData":[OSD([subQ28,subQ27])]})}),subQ34],"blendedInto":[subQ34]});}
            var Q27;
            Q27=makeQuery(id+"F1.opExtrude","CAP_EDGE",EDGE,{"disambiguationData":[OSD([sQuery(id+"F0.wireOp",EDGE,"E10.3")])],"isStart":true});
            var Q28;
            {var subQ0=sQuery(id+"F0.wireOp",EDGE,"E69");var subQ1=sQuery(id+"F0.wireOp",EDGE,"E68");var subQ2=sQuery(id+"F0.wireOp",EDGE,"E66");var subQ3=sQuery(id+"F0.wireOp",EDGE,"E64");var subQ4=sQuery(id+"F0.wireOp",EDGE,"E63");var subQ5=sQuery(id+"F0.wireOp",EDGE,"E62");var subQ6=sQuery(id+"F0.wireOp",EDGE,"E61");var subQ7=sQuery(id+"F0.wireOp",EDGE,"E60");var subQ8=sQuery(id+"F0.wireOp",EDGE,"E55");var subQ9=sQuery(id+"F0.wireOp",EDGE,"E54");var subQ10=sQuery(id+"F0.wireOp",EDGE,"E53");var subQ11=sQuery(id+"F0.wireOp",EDGE,"E52");var subQ12=sQuery(id+"F0.wireOp",EDGE,"E47");var subQ13=sQuery(id+"F0.wireOp",EDGE,"E46");var subQ14=sQuery(id+"F0.wireOp",EDGE,"E45");var subQ15=sQuery(id+"F0.wireOp",EDGE,"E44");var subQ16=sQuery(id+"F0.wireOp",EDGE,"E43");var subQ17=sQuery(id+"F0.wireOp",EDGE,"E42");var subQ18=sQuery(id+"F0.wireOp",EDGE,"E41");var subQ19=sQuery(id+"F0.wireOp",EDGE,"E40");var subQ20=sQuery(id+"F0.wireOp",EDGE,"E26");var subQ21=sQuery(id+"F0.wireOp",EDGE,"E25");var subQ22=sQuery(id+"F0.wireOp",EDGE,"E23");var subQ23=sQuery(id+"F0.wireOp",EDGE,"E20");var subQ24=sQuery(id+"F0.wireOp",EDGE,"E19");var subQ25=sQuery(id+"F0.wireOp",EDGE,"E14");var subQ26=sQuery(id+"F0.wireOp",EDGE,"E12");var subQ27=sQuery(id+"F0.wireOp",EDGE,"E10.3");var subQ28=sQuery(id+"F0.wireOp",EDGE,"E10.2");var subQ29=sQuery(id+"F0.wireOp",EDGE,"E10.1");var subQ30=sQuery(id+"F0.wireOp",EDGE,"E10.0");var subQ31=makeQuery(id+"F1.opExtrude","CAP_FACE",FACE,{"disambiguationData":[OSD([sQuery(id+"F0.wireOp",EDGE,"E6"),sQuery(id+"F0.wireOp",EDGE,"E7"),sQuery(id+"F0.wireOp",EDGE,"E8"),sQuery(id+"F0.wireOp",EDGE,"E9"),subQ30,subQ29,subQ28,subQ27,sQuery(id+"F0.wireOp",EDGE,"E11.0"),sQuery(id+"F0.wireOp",EDGE,"E11.1"),sQuery(id+"F0.wireOp",EDGE,"E11.2"),sQuery(id+"F0.wireOp",EDGE,"E11.3"),subQ26,sQuery(id+"F0.wireOp",EDGE,"E13"),subQ25,sQuery(id+"F0.wireOp",EDGE,"E15"),sQuery(id+"F0.wireOp",EDGE,"E18"),subQ24,subQ23,sQuery(id+"F0.wireOp",EDGE,"E21"),sQuery(id+"F0.wireOp",EDGE,"E22"),subQ22,sQuery(id+"F0.wireOp",EDGE,"E24"),subQ21,subQ20,sQuery(id+"F0.wireOp",EDGE,"E27"),sQuery(id+"F0.wireOp",EDGE,"E32"),sQuery(id+"F0.wireOp",EDGE,"E33"),sQuery(id+"F0.wireOp",EDGE,"E34"),sQuery(id+"F0.wireOp",EDGE,"E35"),sQuery(id+"F0.wireOp",EDGE,"E36"),sQuery(id+"F0.wireOp",EDGE,"E37"),sQuery(id+"F0.wireOp",EDGE,"E38"),sQuery(id+"F0.wireOp",EDGE,"E39"),subQ19,subQ18,subQ17,subQ16,subQ15,subQ14,subQ13,subQ12,sQuery(id+"F0.wireOp",EDGE,"E48"),sQuery(id+"F0.wireOp",EDGE,"E49"),sQuery(id+"F0.wireOp",EDGE,"E50"),sQuery(id+"F0.wireOp",EDGE,"E51"),subQ11,subQ10,subQ9,subQ8,sQuery(id+"F0.wireOp",EDGE,"E56"),sQuery(id+"F0.wireOp",EDGE,"E57"),sQuery(id+"F0.wireOp",EDGE,"E58"),sQuery(id+"F0.wireOp",EDGE,"E59"),subQ7,subQ6,subQ5,subQ4,subQ3,sQuery(id+"F0.wireOp",EDGE,"E65"),subQ2,sQuery(id+"F0.wireOp",EDGE,"E67"),subQ1,subQ0,sQuery(id+"F0.wireOp",EDGE,"E70")])],"isStart":true});Q28=makeQuery(id+"F11.opFillet","BLEND_EDGE",EDGE,{"blendedFrom":[makeQuery(id+"F2.boolean.opBoolean","SPLIT",EDGE,{"disambiguationData":[TD([makeQuery(id+"F2.opExtrude","CAP_FACE",FACE,{"disambiguationData":[OSD([sQuery(id+"F0.wireOp",EDGE,"E4.0"),sQuery(id+"F0.wireOp",EDGE,"E4.1"),sQuery(id+"F0.wireOp",EDGE,"E4.2"),sQuery(id+"F0.wireOp",EDGE,"E4.3"),subQ30,subQ29,subQ28,subQ27,subQ26,subQ25,subQ24,subQ23,subQ22,subQ21,subQ20,subQ19,subQ18,subQ17,subQ16,subQ15,subQ14,subQ13,subQ12,subQ11,subQ10,subQ9,subQ8,subQ7,subQ6,subQ5,subQ4,subQ3,subQ2,subQ1,subQ0])],"isStart":false})])],"derivedFrom":makeQuery(id+"F1.opExtrude","SWEPT_EDGE",EDGE,{"disambiguationData":[OSD([subQ28,subQ27])]})}),subQ31],"blendedInto":[subQ31]});}
            var Q29;
            Q29=makeQuery(id+"F1.opExtrude","CAP_EDGE",EDGE,{"disambiguationData":[OSD([sQuery(id+"F0.wireOp",EDGE,"E10.2")])],"isStart":true});
            var Q30;
            Q30=makeQuery(id+"F1.opExtrude","CAP_EDGE",EDGE,{"disambiguationData":[OSD([sQuery(id+"F0.wireOp",EDGE,"E10.1")])],"isStart":true});
            var Q31;
            {var subQ0=sQuery(id+"F0.wireOp",EDGE,"E69");var subQ1=sQuery(id+"F0.wireOp",EDGE,"E68");var subQ2=sQuery(id+"F0.wireOp",EDGE,"E66");var subQ3=sQuery(id+"F0.wireOp",EDGE,"E64");var subQ4=sQuery(id+"F0.wireOp",EDGE,"E63");var subQ5=sQuery(id+"F0.wireOp",EDGE,"E62");var subQ6=sQuery(id+"F0.wireOp",EDGE,"E61");var subQ7=sQuery(id+"F0.wireOp",EDGE,"E60");var subQ8=sQuery(id+"F0.wireOp",EDGE,"E55");var subQ9=sQuery(id+"F0.wireOp",EDGE,"E54");var subQ10=sQuery(id+"F0.wireOp",EDGE,"E53");var subQ11=sQuery(id+"F0.wireOp",EDGE,"E52");var subQ12=sQuery(id+"F0.wireOp",EDGE,"E47");var subQ13=sQuery(id+"F0.wireOp",EDGE,"E46");var subQ14=sQuery(id+"F0.wireOp",EDGE,"E45");var subQ15=sQuery(id+"F0.wireOp",EDGE,"E44");var subQ16=sQuery(id+"F0.wireOp",EDGE,"E43");var subQ17=sQuery(id+"F0.wireOp",EDGE,"E42");var subQ18=sQuery(id+"F0.wireOp",EDGE,"E41");var subQ19=sQuery(id+"F0.wireOp",EDGE,"E40");var subQ20=sQuery(id+"F0.wireOp",EDGE,"E26");var subQ21=sQuery(id+"F0.wireOp",EDGE,"E25");var subQ22=sQuery(id+"F0.wireOp",EDGE,"E23");var subQ23=sQuery(id+"F0.wireOp",EDGE,"E20");var subQ24=sQuery(id+"F0.wireOp",EDGE,"E19");var subQ25=sQuery(id+"F0.wireOp",EDGE,"E14");var subQ26=sQuery(id+"F0.wireOp",EDGE,"E12");var subQ27=sQuery(id+"F0.wireOp",EDGE,"E10.3");var subQ28=sQuery(id+"F0.wireOp",EDGE,"E10.2");var subQ29=sQuery(id+"F0.wireOp",EDGE,"E10.1");var subQ30=sQuery(id+"F0.wireOp",EDGE,"E10.0");var subQ31=makeQuery(id+"F1.opExtrude","CAP_FACE",FACE,{"disambiguationData":[OSD([sQuery(id+"F0.wireOp",EDGE,"E6"),sQuery(id+"F0.wireOp",EDGE,"E7"),sQuery(id+"F0.wireOp",EDGE,"E8"),sQuery(id+"F0.wireOp",EDGE,"E9"),subQ30,subQ29,subQ28,subQ27,sQuery(id+"F0.wireOp",EDGE,"E11.0"),sQuery(id+"F0.wireOp",EDGE,"E11.1"),sQuery(id+"F0.wireOp",EDGE,"E11.2"),sQuery(id+"F0.wireOp",EDGE,"E11.3"),subQ26,sQuery(id+"F0.wireOp",EDGE,"E13"),subQ25,sQuery(id+"F0.wireOp",EDGE,"E15"),sQuery(id+"F0.wireOp",EDGE,"E18"),subQ24,subQ23,sQuery(id+"F0.wireOp",EDGE,"E21"),sQuery(id+"F0.wireOp",EDGE,"E22"),subQ22,sQuery(id+"F0.wireOp",EDGE,"E24"),subQ21,subQ20,sQuery(id+"F0.wireOp",EDGE,"E27"),sQuery(id+"F0.wireOp",EDGE,"E32"),sQuery(id+"F0.wireOp",EDGE,"E33"),sQuery(id+"F0.wireOp",EDGE,"E34"),sQuery(id+"F0.wireOp",EDGE,"E35"),sQuery(id+"F0.wireOp",EDGE,"E36"),sQuery(id+"F0.wireOp",EDGE,"E37"),sQuery(id+"F0.wireOp",EDGE,"E38"),sQuery(id+"F0.wireOp",EDGE,"E39"),subQ19,subQ18,subQ17,subQ16,subQ15,subQ14,subQ13,subQ12,sQuery(id+"F0.wireOp",EDGE,"E48"),sQuery(id+"F0.wireOp",EDGE,"E49"),sQuery(id+"F0.wireOp",EDGE,"E50"),sQuery(id+"F0.wireOp",EDGE,"E51"),subQ11,subQ10,subQ9,subQ8,sQuery(id+"F0.wireOp",EDGE,"E56"),sQuery(id+"F0.wireOp",EDGE,"E57"),sQuery(id+"F0.wireOp",EDGE,"E58"),sQuery(id+"F0.wireOp",EDGE,"E59"),subQ7,subQ6,subQ5,subQ4,subQ3,sQuery(id+"F0.wireOp",EDGE,"E65"),subQ2,sQuery(id+"F0.wireOp",EDGE,"E67"),subQ1,subQ0,sQuery(id+"F0.wireOp",EDGE,"E70")])],"isStart":true});Q31=makeQuery(id+"F11.opFillet","BLEND_EDGE",EDGE,{"blendedFrom":[makeQuery(id+"F2.boolean.opBoolean","SPLIT",EDGE,{"disambiguationData":[TD([makeQuery(id+"F2.opExtrude","CAP_FACE",FACE,{"disambiguationData":[OSD([sQuery(id+"F0.wireOp",EDGE,"E4.0"),sQuery(id+"F0.wireOp",EDGE,"E4.1"),sQuery(id+"F0.wireOp",EDGE,"E4.2"),sQuery(id+"F0.wireOp",EDGE,"E4.3"),subQ30,subQ29,subQ28,subQ27,subQ26,subQ25,subQ24,subQ23,subQ22,subQ21,subQ20,subQ19,subQ18,subQ17,subQ16,subQ15,subQ14,subQ13,subQ12,subQ11,subQ10,subQ9,subQ8,subQ7,subQ6,subQ5,subQ4,subQ3,subQ2,subQ1,subQ0])],"isStart":false})])],"derivedFrom":makeQuery(id+"F1.opExtrude","SWEPT_EDGE",EDGE,{"disambiguationData":[OSD([subQ30,subQ29])]})}),subQ31],"blendedInto":[subQ31]});}
            var Q32;
            Q32=makeQuery(id+"F1.opExtrude","CAP_EDGE",EDGE,{"disambiguationData":[OSD([sQuery(id+"F0.wireOp",EDGE,"E10.0")])],"isStart":true});
            var Q33;
            {var subQ0=sQuery(id+"F0.wireOp",EDGE,"E69");var subQ1=sQuery(id+"F0.wireOp",EDGE,"E68");var subQ2=sQuery(id+"F0.wireOp",EDGE,"E66");var subQ3=sQuery(id+"F0.wireOp",EDGE,"E64");var subQ4=sQuery(id+"F0.wireOp",EDGE,"E63");var subQ5=sQuery(id+"F0.wireOp",EDGE,"E62");var subQ6=sQuery(id+"F0.wireOp",EDGE,"E61");var subQ7=sQuery(id+"F0.wireOp",EDGE,"E60");var subQ8=sQuery(id+"F0.wireOp",EDGE,"E55");var subQ9=sQuery(id+"F0.wireOp",EDGE,"E54");var subQ10=sQuery(id+"F0.wireOp",EDGE,"E53");var subQ11=sQuery(id+"F0.wireOp",EDGE,"E52");var subQ12=sQuery(id+"F0.wireOp",EDGE,"E47");var subQ13=sQuery(id+"F0.wireOp",EDGE,"E46");var subQ14=sQuery(id+"F0.wireOp",EDGE,"E45");var subQ15=sQuery(id+"F0.wireOp",EDGE,"E44");var subQ16=sQuery(id+"F0.wireOp",EDGE,"E43");var subQ17=sQuery(id+"F0.wireOp",EDGE,"E42");var subQ18=sQuery(id+"F0.wireOp",EDGE,"E41");var subQ19=sQuery(id+"F0.wireOp",EDGE,"E40");var subQ20=sQuery(id+"F0.wireOp",EDGE,"E26");var subQ21=sQuery(id+"F0.wireOp",EDGE,"E25");var subQ22=sQuery(id+"F0.wireOp",EDGE,"E23");var subQ23=sQuery(id+"F0.wireOp",EDGE,"E20");var subQ24=sQuery(id+"F0.wireOp",EDGE,"E19");var subQ25=sQuery(id+"F0.wireOp",EDGE,"E15");var subQ26=sQuery(id+"F0.wireOp",EDGE,"E14");var subQ27=sQuery(id+"F0.wireOp",EDGE,"E12");var subQ28=sQuery(id+"F0.wireOp",EDGE,"E10.3");var subQ29=sQuery(id+"F0.wireOp",EDGE,"E10.2");var subQ30=sQuery(id+"F0.wireOp",EDGE,"E10.1");var subQ31=sQuery(id+"F0.wireOp",EDGE,"E10.0");var subQ32=sQuery(id+"F0.wireOp",EDGE,"E9");var subQ33=sQuery(id+"F0.wireOp",EDGE,"E8");var subQ34=makeQuery(id+"F1.opExtrude","CAP_FACE",FACE,{"disambiguationData":[OSD([sQuery(id+"F0.wireOp",EDGE,"E6"),sQuery(id+"F0.wireOp",EDGE,"E7"),subQ33,subQ32,subQ31,subQ30,subQ29,subQ28,sQuery(id+"F0.wireOp",EDGE,"E11.0"),sQuery(id+"F0.wireOp",EDGE,"E11.1"),sQuery(id+"F0.wireOp",EDGE,"E11.2"),sQuery(id+"F0.wireOp",EDGE,"E11.3"),subQ27,sQuery(id+"F0.wireOp",EDGE,"E13"),subQ26,subQ25,sQuery(id+"F0.wireOp",EDGE,"E18"),subQ24,subQ23,sQuery(id+"F0.wireOp",EDGE,"E21"),sQuery(id+"F0.wireOp",EDGE,"E22"),subQ22,sQuery(id+"F0.wireOp",EDGE,"E24"),subQ21,subQ20,sQuery(id+"F0.wireOp",EDGE,"E27"),sQuery(id+"F0.wireOp",EDGE,"E32"),sQuery(id+"F0.wireOp",EDGE,"E33"),sQuery(id+"F0.wireOp",EDGE,"E34"),sQuery(id+"F0.wireOp",EDGE,"E35"),sQuery(id+"F0.wireOp",EDGE,"E36"),sQuery(id+"F0.wireOp",EDGE,"E37"),sQuery(id+"F0.wireOp",EDGE,"E38"),sQuery(id+"F0.wireOp",EDGE,"E39"),subQ19,subQ18,subQ17,subQ16,subQ15,subQ14,subQ13,subQ12,sQuery(id+"F0.wireOp",EDGE,"E48"),sQuery(id+"F0.wireOp",EDGE,"E49"),sQuery(id+"F0.wireOp",EDGE,"E50"),sQuery(id+"F0.wireOp",EDGE,"E51"),subQ11,subQ10,subQ9,subQ8,sQuery(id+"F0.wireOp",EDGE,"E56"),sQuery(id+"F0.wireOp",EDGE,"E57"),sQuery(id+"F0.wireOp",EDGE,"E58"),sQuery(id+"F0.wireOp",EDGE,"E59"),subQ7,subQ6,subQ5,subQ4,subQ3,sQuery(id+"F0.wireOp",EDGE,"E65"),subQ2,sQuery(id+"F0.wireOp",EDGE,"E67"),subQ1,subQ0,sQuery(id+"F0.wireOp",EDGE,"E70")])],"isStart":true});Q33=makeQuery(id+"F11.opFillet","BLEND_EDGE",EDGE,{"blendedFrom":[makeQuery(id+"F2.boolean.opBoolean","SPLIT",EDGE,{"disambiguationData":[TD([makeQuery(id+"F2.opExtrude","CAP_FACE",FACE,{"disambiguationData":[OSD([sQuery(id+"F0.wireOp",EDGE,"E4.0"),sQuery(id+"F0.wireOp",EDGE,"E4.1"),sQuery(id+"F0.wireOp",EDGE,"E4.2"),sQuery(id+"F0.wireOp",EDGE,"E4.3"),subQ31,subQ30,subQ29,subQ28,subQ27,subQ26,subQ24,subQ23,subQ22,subQ21,subQ20,subQ19,subQ18,subQ17,subQ16,subQ15,subQ14,subQ13,subQ12,subQ11,subQ10,subQ9,subQ8,subQ7,subQ6,subQ5,subQ4,subQ3,subQ2,subQ1,subQ0])],"isStart":false})])],"derivedFrom":makeQuery(id+"F1.opExtrude","SWEPT_EDGE",EDGE,{"disambiguationData":[OSD([subQ31,subQ26])]})}),subQ34],"blendedInto":[subQ34]});}
            chamfer(context, id + "F13", {"entities" : qUnion([Q0, Q1, Q2, Q3, Q4, Q5, Q6, Q7, Q8, Q9, Q10, Q11, Q12, Q13, Q14, Q15, Q16, Q17, Q18, Q19, Q20, Q21, Q22, Q23, Q24, Q25, Q26, Q27, Q28, Q29, Q30, Q31, Q32, Q33]), "width" : 1 * mm, "tangentPropagation" : true});
        }
    });
